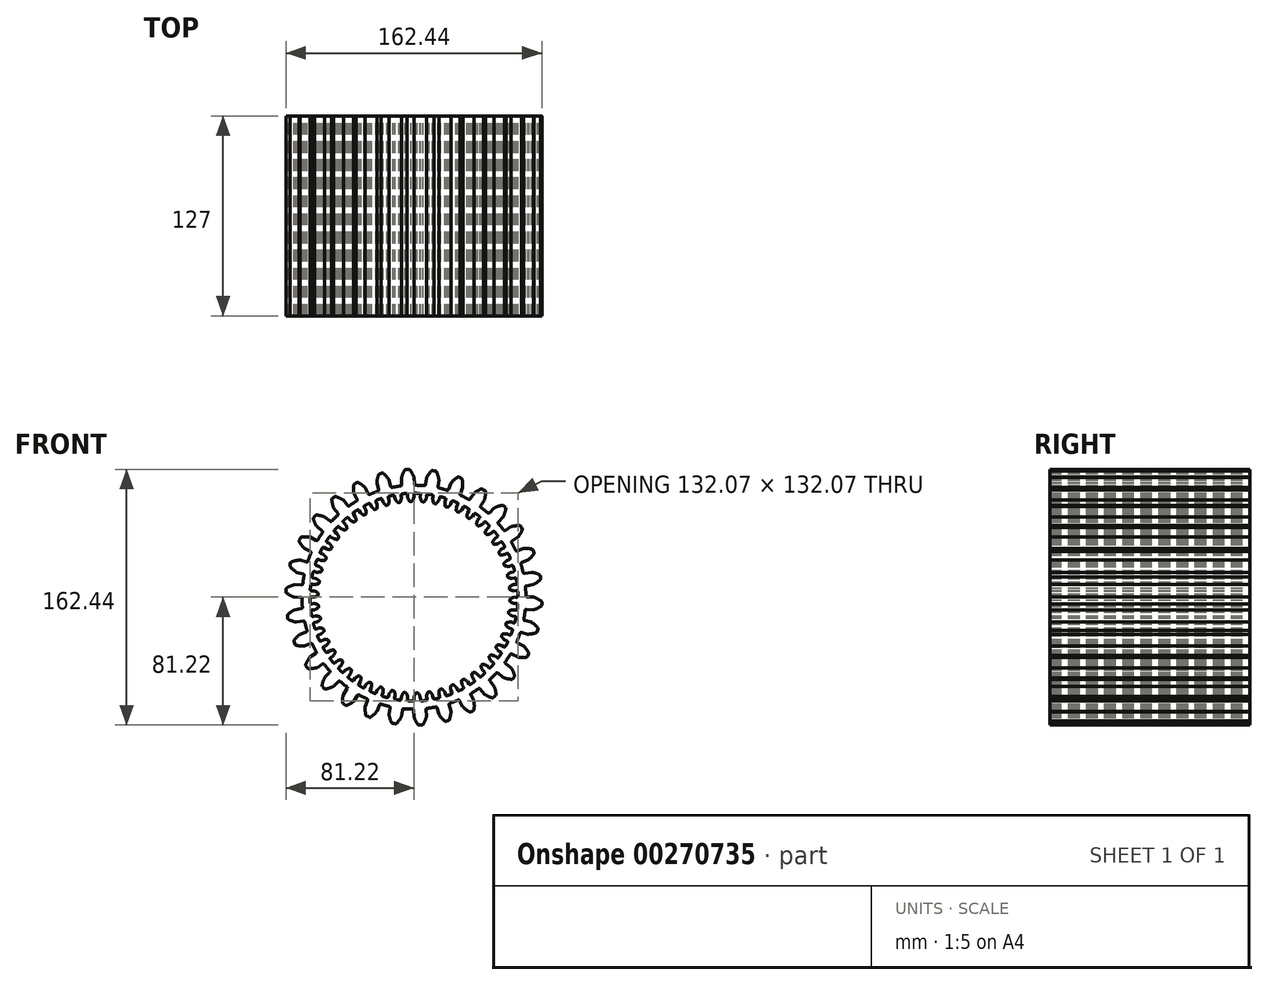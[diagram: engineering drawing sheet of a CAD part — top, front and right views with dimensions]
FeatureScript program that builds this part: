
annotation { "Feature Type Name" : "Feature", "Feature Type Description" : "" }
export const myFeature = defineFeature(function(context is Context, id is Id, definition is map)
    precondition{}
    {
        {
            var Q0;
            Q0=qCreatedBy(makeId("Front.planeOp"),FACE);
            var sketch = newSketch(context, id + "F0", { "sketchPlane" : qUnion([Q0])});
            skArc(sketch, "E0", {"start": v(-8.43, 70.62) * mm, "mid": v(-11.13, 70.24) * mm, "end": v(-13.8, 69.77) * mm});
            skArc(sketch, "E1", {"start": v(0, 76.2) * mm, "mid": v(-1.15, 78.65) * mm, "end": v(-2.63, 80.9) * mm});
            skLineSegment(sketch, "E2", {"start": v(-3.28, 81.21) * mm, "end": v(-4.25, 81.18) * mm});
            skLineSegment(sketch, "E3", {"start": v(0, 76.2) * mm, "end": v(0.23, 71.86) * mm});
            skLineSegment(sketch, "E4.MirrorCS", {"start": v(-5.23, 81.11) * mm, "end": v(-4.25, 81.18) * mm});
            skArc(sketch, "E5.MirrorCS", {"start": v(-7.97, 75.78) * mm, "mid": v(-7.08, 78.33) * mm, "end": v(-5.85, 80.74) * mm});
            skLineSegment(sketch, "E6.MirrorCS", {"start": v(-7.97, 75.78) * mm, "end": v(-7.74, 71.44) * mm});
            skPoint(sketch, "E7.visualSharp", {"position": v(-7.7, 70.7) * mm});
            skArc(sketch, "E7.filletArc", {"start": v(-8.43, 70.62) * mm, "mid": v(-7.92, 70.9) * mm, "end": v(-7.74, 71.44) * mm});
            skPoint(sketch, "E8.visualSharp", {"position": v(0.27, 71.12) * mm});
            skArc(sketch, "E8.filletArc", {"start": v(0.23, 71.86) * mm, "mid": v(0.47, 71.33) * mm, "end": v(1, 71.11) * mm});
            skPoint(sketch, "E9.visualSharp", {"position": v(-5.63, 81.08) * mm});
            skArc(sketch, "E9.filletArc", {"start": v(-5.23, 81.11) * mm, "mid": v(-5.58, 81) * mm, "end": v(-5.85, 80.74) * mm});
            skPoint(sketch, "E10.visualSharp", {"position": v(-2.88, 81.23) * mm});
            skArc(sketch, "E10.filletArc", {"start": v(-2.63, 80.9) * mm, "mid": v(-2.92, 81.14) * mm, "end": v(-3.28, 81.21) * mm});
            skArc(sketch, "E11.1.0", {"start": v(-22.93, 67.32) * mm, "mid": v(-22.49, 67.7) * mm, "end": v(-22.42, 68.27) * mm});
            skArc(sketch, "E11.1.1", {"start": v(-23.55, 72.47) * mm, "mid": v(-23.21, 75.15) * mm, "end": v(-22.5, 77.76) * mm});
            skArc(sketch, "E11.1.2", {"start": v(-21.98, 78.25) * mm, "mid": v(-22.3, 78.07) * mm, "end": v(-22.5, 77.76) * mm});
            skLineSegment(sketch, "E11.1.3", {"start": v(-21.98, 78.25) * mm, "end": v(-21.04, 78.52) * mm});
            skLineSegment(sketch, "E11.1.4", {"start": v(-20.1, 78.76) * mm, "end": v(-21.04, 78.52) * mm});
            skArc(sketch, "E11.1.5", {"start": v(-19.39, 78.6) * mm, "mid": v(-19.72, 78.76) * mm, "end": v(-20.1, 78.76) * mm});
            skArc(sketch, "E11.1.6", {"start": v(-15.84, 74.53) * mm, "mid": v(-17.47, 76.69) * mm, "end": v(-19.39, 78.6) * mm});
            skArc(sketch, "E11.1.7", {"start": v(-14.72, 70.34) * mm, "mid": v(-14.37, 69.87) * mm, "end": v(-13.8, 69.77) * mm});
            skLineSegment(sketch, "E11.1.8", {"start": v(-15.84, 74.53) * mm, "end": v(-14.72, 70.34) * mm});
            skLineSegment(sketch, "E11.1.9", {"start": v(-23.55, 72.47) * mm, "end": v(-22.42, 68.27) * mm});
            skArc(sketch, "E11.2.0", {"start": v(-36.42, 61.08) * mm, "mid": v(-36.07, 61.54) * mm, "end": v(-36.13, 62.12) * mm});
            skArc(sketch, "E11.2.1", {"start": v(-38.1, 66) * mm, "mid": v(-38.33, 68.68) * mm, "end": v(-38.18, 71.38) * mm});
            skArc(sketch, "E11.2.2", {"start": v(-37.77, 71.97) * mm, "mid": v(-38.05, 71.73) * mm, "end": v(-38.18, 71.38) * mm});
            skLineSegment(sketch, "E11.2.3", {"start": v(-37.77, 71.97) * mm, "end": v(-36.9, 72.43) * mm});
            skLineSegment(sketch, "E11.2.4", {"start": v(-36.03, 72.86) * mm, "end": v(-36.9, 72.43) * mm});
            skArc(sketch, "E11.2.5", {"start": v(-35.3, 72.84) * mm, "mid": v(-35.67, 72.94) * mm, "end": v(-36.03, 72.86) * mm});
            skArc(sketch, "E11.2.6", {"start": v(-31, 69.61) * mm, "mid": v(-33.03, 71.38) * mm, "end": v(-35.3, 72.84) * mm});
            skArc(sketch, "E11.2.7", {"start": v(-29.02, 65.74) * mm, "mid": v(-28.59, 65.36) * mm, "end": v(-28, 65.37) * mm});
            skLineSegment(sketch, "E11.2.8", {"start": v(-31, 69.61) * mm, "end": v(-29.02, 65.74) * mm});
            skLineSegment(sketch, "E11.2.9", {"start": v(-38.1, 66) * mm, "end": v(-36.13, 62.12) * mm});
            skArc(sketch, "E11.3.0", {"start": v(-48.33, 52.18) * mm, "mid": v(-48.08, 52.7) * mm, "end": v(-48.25, 53.25) * mm});
            skArc(sketch, "E11.3.1", {"start": v(-50.99, 56.63) * mm, "mid": v(-51.77, 59.21) * mm, "end": v(-52.18, 61.88) * mm});
            skArc(sketch, "E11.3.2", {"start": v(-51.9, 62.55) * mm, "mid": v(-52.13, 62.25) * mm, "end": v(-52.18, 61.88) * mm});
            skLineSegment(sketch, "E11.3.3", {"start": v(-51.9, 62.55) * mm, "end": v(-51.16, 63.18) * mm});
            skLineSegment(sketch, "E11.3.4", {"start": v(-50.4, 63.78) * mm, "end": v(-51.16, 63.18) * mm});
            skArc(sketch, "E11.3.5", {"start": v(-49.68, 63.91) * mm, "mid": v(-50.05, 63.93) * mm, "end": v(-50.4, 63.78) * mm});
            skArc(sketch, "E11.3.6", {"start": v(-44.79, 61.65) * mm, "mid": v(-47.15, 62.95) * mm, "end": v(-49.68, 63.91) * mm});
            skArc(sketch, "E11.3.7", {"start": v(-42.05, 58.27) * mm, "mid": v(-41.55, 57.98) * mm, "end": v(-40.99, 58.12) * mm});
            skLineSegment(sketch, "E11.3.8", {"start": v(-44.79, 61.65) * mm, "end": v(-42.05, 58.27) * mm});
            skLineSegment(sketch, "E11.3.9", {"start": v(-50.99, 56.63) * mm, "end": v(-48.25, 53.25) * mm});
            skArc(sketch, "E11.4.0", {"start": v(-58.12, 40.99) * mm, "mid": v(-57.98, 41.55) * mm, "end": v(-58.27, 42.05) * mm});
            skArc(sketch, "E11.4.1", {"start": v(-61.65, 44.79) * mm, "mid": v(-62.95, 47.15) * mm, "end": v(-63.91, 49.68) * mm});
            skArc(sketch, "E11.4.2", {"start": v(-63.78, 50.4) * mm, "mid": v(-63.93, 50.05) * mm, "end": v(-63.91, 49.68) * mm});
            skLineSegment(sketch, "E11.4.3", {"start": v(-63.78, 50.4) * mm, "end": v(-63.18, 51.16) * mm});
            skLineSegment(sketch, "E11.4.4", {"start": v(-62.55, 51.9) * mm, "end": v(-63.18, 51.16) * mm});
            skArc(sketch, "E11.4.5", {"start": v(-61.88, 52.18) * mm, "mid": v(-62.25, 52.13) * mm, "end": v(-62.55, 51.9) * mm});
            skArc(sketch, "E11.4.6", {"start": v(-56.63, 50.99) * mm, "mid": v(-59.21, 51.77) * mm, "end": v(-61.88, 52.18) * mm});
            skArc(sketch, "E11.4.7", {"start": v(-53.25, 48.25) * mm, "mid": v(-52.7, 48.08) * mm, "end": v(-52.18, 48.33) * mm});
            skLineSegment(sketch, "E11.4.8", {"start": v(-56.63, 50.99) * mm, "end": v(-53.25, 48.25) * mm});
            skLineSegment(sketch, "E11.4.9", {"start": v(-61.65, 44.79) * mm, "end": v(-58.27, 42.05) * mm});
            skArc(sketch, "E11.5.0", {"start": v(-65.37, 28) * mm, "mid": v(-65.36, 28.59) * mm, "end": v(-65.74, 29.02) * mm});
            skArc(sketch, "E11.5.1", {"start": v(-69.61, 31) * mm, "mid": v(-71.38, 33.03) * mm, "end": v(-72.84, 35.3) * mm});
            skArc(sketch, "E11.5.2", {"start": v(-72.86, 36.03) * mm, "mid": v(-72.94, 35.67) * mm, "end": v(-72.84, 35.3) * mm});
            skLineSegment(sketch, "E11.5.3", {"start": v(-72.86, 36.03) * mm, "end": v(-72.43, 36.9) * mm});
            skLineSegment(sketch, "E11.5.4", {"start": v(-71.97, 37.77) * mm, "end": v(-72.43, 36.9) * mm});
            skArc(sketch, "E11.5.5", {"start": v(-71.38, 38.18) * mm, "mid": v(-71.73, 38.05) * mm, "end": v(-71.97, 37.77) * mm});
            skArc(sketch, "E11.5.6", {"start": v(-66, 38.1) * mm, "mid": v(-68.68, 38.33) * mm, "end": v(-71.38, 38.18) * mm});
            skArc(sketch, "E11.5.7", {"start": v(-62.12, 36.13) * mm, "mid": v(-61.54, 36.07) * mm, "end": v(-61.08, 36.42) * mm});
            skLineSegment(sketch, "E11.5.8", {"start": v(-66, 38.1) * mm, "end": v(-62.12, 36.13) * mm});
            skLineSegment(sketch, "E11.5.9", {"start": v(-69.61, 31) * mm, "end": v(-65.74, 29.02) * mm});
            skArc(sketch, "E11.6.0", {"start": v(-69.77, 13.8) * mm, "mid": v(-69.87, 14.37) * mm, "end": v(-70.34, 14.72) * mm});
            skArc(sketch, "E11.6.1", {"start": v(-74.53, 15.84) * mm, "mid": v(-76.69, 17.47) * mm, "end": v(-78.6, 19.39) * mm});
            skArc(sketch, "E11.6.2", {"start": v(-78.76, 20.1) * mm, "mid": v(-78.76, 19.72) * mm, "end": v(-78.6, 19.39) * mm});
            skLineSegment(sketch, "E11.6.3", {"start": v(-78.76, 20.1) * mm, "end": v(-78.52, 21.04) * mm});
            skLineSegment(sketch, "E11.6.4", {"start": v(-78.25, 21.98) * mm, "end": v(-78.52, 21.04) * mm});
            skArc(sketch, "E11.6.5", {"start": v(-77.76, 22.5) * mm, "mid": v(-78.07, 22.3) * mm, "end": v(-78.25, 21.98) * mm});
            skArc(sketch, "E11.6.6", {"start": v(-72.47, 23.55) * mm, "mid": v(-75.15, 23.21) * mm, "end": v(-77.76, 22.5) * mm});
            skArc(sketch, "E11.6.7", {"start": v(-68.27, 22.42) * mm, "mid": v(-67.7, 22.49) * mm, "end": v(-67.32, 22.93) * mm});
            skLineSegment(sketch, "E11.6.8", {"start": v(-72.47, 23.55) * mm, "end": v(-68.27, 22.42) * mm});
            skLineSegment(sketch, "E11.6.9", {"start": v(-74.53, 15.84) * mm, "end": v(-70.34, 14.72) * mm});
            skArc(sketch, "E11.7.0", {"start": v(-71.11, -1) * mm, "mid": v(-71.33, -0.47) * mm, "end": v(-71.86, -0.23) * mm});
            skArc(sketch, "E11.7.1", {"start": v(-76.2, 0) * mm, "mid": v(-78.65, 1.15) * mm, "end": v(-80.9, 2.63) * mm});
            skArc(sketch, "E11.7.2", {"start": v(-81.21, 3.28) * mm, "mid": v(-81.14, 2.92) * mm, "end": v(-80.9, 2.63) * mm});
            skLineSegment(sketch, "E11.7.3", {"start": v(-81.21, 3.28) * mm, "end": v(-81.18, 4.25) * mm});
            skLineSegment(sketch, "E11.7.4", {"start": v(-81.11, 5.23) * mm, "end": v(-81.18, 4.25) * mm});
            skArc(sketch, "E11.7.5", {"start": v(-80.74, 5.85) * mm, "mid": v(-81, 5.58) * mm, "end": v(-81.11, 5.23) * mm});
            skArc(sketch, "E11.7.6", {"start": v(-75.78, 7.97) * mm, "mid": v(-78.33, 7.08) * mm, "end": v(-80.74, 5.85) * mm});
            skArc(sketch, "E11.7.7", {"start": v(-71.44, 7.74) * mm, "mid": v(-70.9, 7.92) * mm, "end": v(-70.62, 8.43) * mm});
            skLineSegment(sketch, "E11.7.8", {"start": v(-75.78, 7.97) * mm, "end": v(-71.44, 7.74) * mm});
            skLineSegment(sketch, "E11.7.9", {"start": v(-76.2, 0) * mm, "end": v(-71.86, -0.23) * mm});
            skArc(sketch, "E11.8.0", {"start": v(-69.35, -15.77) * mm, "mid": v(-69.68, -15.29) * mm, "end": v(-70.24, -15.16) * mm});
            skArc(sketch, "E11.8.1", {"start": v(-74.53, -15.84) * mm, "mid": v(-77.17, -15.23) * mm, "end": v(-79.68, -14.25) * mm});
            skArc(sketch, "E11.8.2", {"start": v(-80.12, -13.68) * mm, "mid": v(-79.97, -14.02) * mm, "end": v(-79.68, -14.25) * mm});
            skLineSegment(sketch, "E11.8.3", {"start": v(-80.12, -13.68) * mm, "end": v(-80.3, -12.72) * mm});
            skLineSegment(sketch, "E11.8.4", {"start": v(-80.43, -11.75) * mm, "end": v(-80.3, -12.72) * mm});
            skArc(sketch, "E11.8.5", {"start": v(-80.19, -11.07) * mm, "mid": v(-80.4, -11.38) * mm, "end": v(-80.43, -11.75) * mm});
            skArc(sketch, "E11.8.6", {"start": v(-75.78, -7.97) * mm, "mid": v(-78.1, -9.36) * mm, "end": v(-80.19, -11.07) * mm});
            skArc(sketch, "E11.8.7", {"start": v(-71.49, -7.29) * mm, "mid": v(-71, -7) * mm, "end": v(-70.83, -6.44) * mm});
            skLineSegment(sketch, "E11.8.8", {"start": v(-75.78, -7.97) * mm, "end": v(-71.49, -7.29) * mm});
            skLineSegment(sketch, "E11.8.9", {"start": v(-74.53, -15.84) * mm, "end": v(-70.24, -15.16) * mm});
            skArc(sketch, "E11.9.0", {"start": v(-64.56, -29.84) * mm, "mid": v(-64.98, -29.44) * mm, "end": v(-65.55, -29.44) * mm});
            skArc(sketch, "E11.9.1", {"start": v(-69.61, -31) * mm, "mid": v(-72.31, -30.94) * mm, "end": v(-74.98, -30.5) * mm});
            skArc(sketch, "E11.9.2", {"start": v(-75.53, -30.04) * mm, "mid": v(-75.31, -30.34) * mm, "end": v(-74.98, -30.5) * mm});
            skLineSegment(sketch, "E11.9.3", {"start": v(-75.53, -30.04) * mm, "end": v(-75.9, -29.13) * mm});
            skLineSegment(sketch, "E11.9.4", {"start": v(-76.23, -28.22) * mm, "end": v(-75.9, -29.13) * mm});
            skArc(sketch, "E11.9.5", {"start": v(-76.13, -27.5) * mm, "mid": v(-76.27, -27.85) * mm, "end": v(-76.23, -28.22) * mm});
            skArc(sketch, "E11.9.6", {"start": v(-72.47, -23.55) * mm, "mid": v(-74.44, -25.4) * mm, "end": v(-76.13, -27.5) * mm});
            skArc(sketch, "E11.9.7", {"start": v(-68.41, -21.99) * mm, "mid": v(-67.99, -21.6) * mm, "end": v(-67.94, -21.02) * mm});
            skLineSegment(sketch, "E11.9.8", {"start": v(-72.47, -23.55) * mm, "end": v(-68.41, -21.99) * mm});
            skLineSegment(sketch, "E11.9.9", {"start": v(-69.61, -31) * mm, "end": v(-65.55, -29.44) * mm});
            skArc(sketch, "E11.10.0", {"start": v(-56.94, -42.61) * mm, "mid": v(-57.43, -42.3) * mm, "end": v(-58, -42.42) * mm});
            skArc(sketch, "E11.10.1", {"start": v(-61.65, -44.79) * mm, "mid": v(-64.3, -45.3) * mm, "end": v(-67, -45.43) * mm});
            skArc(sketch, "E11.10.2", {"start": v(-67.63, -45.08) * mm, "mid": v(-67.36, -45.33) * mm, "end": v(-67, -45.43) * mm});
            skLineSegment(sketch, "E11.10.3", {"start": v(-67.63, -45.08) * mm, "end": v(-68.18, -44.27) * mm});
            skLineSegment(sketch, "E11.10.4", {"start": v(-68.7, -43.45) * mm, "end": v(-68.18, -44.27) * mm});
            skArc(sketch, "E11.10.5", {"start": v(-68.75, -42.73) * mm, "mid": v(-68.81, -43.1) * mm, "end": v(-68.7, -43.45) * mm});
            skArc(sketch, "E11.10.6", {"start": v(-66, -38.1) * mm, "mid": v(-67.54, -40.32) * mm, "end": v(-68.75, -42.73) * mm});
            skArc(sketch, "E11.10.7", {"start": v(-62.35, -35.73) * mm, "mid": v(-62.01, -35.26) * mm, "end": v(-62.09, -34.69) * mm});
            skLineSegment(sketch, "E11.10.8", {"start": v(-66, -38.1) * mm, "end": v(-62.35, -35.73) * mm});
            skLineSegment(sketch, "E11.10.9", {"start": v(-61.65, -44.79) * mm, "end": v(-58, -42.42) * mm});
            skArc(sketch, "E11.11.0", {"start": v(-46.84, -53.52) * mm, "mid": v(-47.38, -53.32) * mm, "end": v(-47.91, -53.55) * mm});
            skArc(sketch, "E11.11.1", {"start": v(-50.99, -56.63) * mm, "mid": v(-53.48, -57.68) * mm, "end": v(-56.09, -58.37) * mm});
            skArc(sketch, "E11.11.2", {"start": v(-56.78, -58.16) * mm, "mid": v(-56.46, -58.35) * mm, "end": v(-56.09, -58.37) * mm});
            skLineSegment(sketch, "E11.11.3", {"start": v(-56.78, -58.16) * mm, "end": v(-57.48, -57.48) * mm});
            skLineSegment(sketch, "E11.11.4", {"start": v(-58.16, -56.78) * mm, "end": v(-57.48, -57.48) * mm});
            skArc(sketch, "E11.11.5", {"start": v(-58.37, -56.09) * mm, "mid": v(-58.35, -56.46) * mm, "end": v(-58.16, -56.78) * mm});
            skArc(sketch, "E11.11.6", {"start": v(-56.63, -50.99) * mm, "mid": v(-57.68, -53.48) * mm, "end": v(-58.37, -56.09) * mm});
            skArc(sketch, "E11.11.7", {"start": v(-53.55, -47.91) * mm, "mid": v(-53.32, -47.38) * mm, "end": v(-53.52, -46.84) * mm});
            skLineSegment(sketch, "E11.11.8", {"start": v(-56.63, -50.99) * mm, "end": v(-53.55, -47.91) * mm});
            skLineSegment(sketch, "E11.11.9", {"start": v(-50.99, -56.63) * mm, "end": v(-47.91, -53.55) * mm});
            skArc(sketch, "E11.12.0", {"start": v(-34.69, -62.09) * mm, "mid": v(-35.26, -62.01) * mm, "end": v(-35.73, -62.35) * mm});
            skArc(sketch, "E11.12.1", {"start": v(-38.1, -66) * mm, "mid": v(-40.32, -67.54) * mm, "end": v(-42.73, -68.75) * mm});
            skArc(sketch, "E11.12.2", {"start": v(-43.45, -68.7) * mm, "mid": v(-43.1, -68.81) * mm, "end": v(-42.73, -68.75) * mm});
            skLineSegment(sketch, "E11.12.3", {"start": v(-43.45, -68.7) * mm, "end": v(-44.27, -68.18) * mm});
            skLineSegment(sketch, "E11.12.4", {"start": v(-45.08, -67.63) * mm, "end": v(-44.27, -68.18) * mm});
            skArc(sketch, "E11.12.5", {"start": v(-45.43, -67) * mm, "mid": v(-45.33, -67.36) * mm, "end": v(-45.08, -67.63) * mm});
            skArc(sketch, "E11.12.6", {"start": v(-44.79, -61.65) * mm, "mid": v(-45.3, -64.3) * mm, "end": v(-45.43, -67) * mm});
            skArc(sketch, "E11.12.7", {"start": v(-42.42, -58) * mm, "mid": v(-42.3, -57.43) * mm, "end": v(-42.61, -56.94) * mm});
            skLineSegment(sketch, "E11.12.8", {"start": v(-44.79, -61.65) * mm, "end": v(-42.42, -58) * mm});
            skLineSegment(sketch, "E11.12.9", {"start": v(-38.1, -66) * mm, "end": v(-35.73, -62.35) * mm});
            skArc(sketch, "E11.13.0", {"start": v(-21.02, -67.94) * mm, "mid": v(-21.6, -67.99) * mm, "end": v(-21.99, -68.41) * mm});
            skArc(sketch, "E11.13.1", {"start": v(-23.55, -72.47) * mm, "mid": v(-25.4, -74.44) * mm, "end": v(-27.5, -76.13) * mm});
            skArc(sketch, "E11.13.2", {"start": v(-28.22, -76.23) * mm, "mid": v(-27.85, -76.27) * mm, "end": v(-27.5, -76.13) * mm});
            skLineSegment(sketch, "E11.13.3", {"start": v(-28.22, -76.23) * mm, "end": v(-29.13, -75.9) * mm});
            skLineSegment(sketch, "E11.13.4", {"start": v(-30.04, -75.53) * mm, "end": v(-29.13, -75.9) * mm});
            skArc(sketch, "E11.13.5", {"start": v(-30.5, -74.98) * mm, "mid": v(-30.34, -75.31) * mm, "end": v(-30.04, -75.53) * mm});
            skArc(sketch, "E11.13.6", {"start": v(-31, -69.61) * mm, "mid": v(-30.94, -72.31) * mm, "end": v(-30.5, -74.98) * mm});
            skArc(sketch, "E11.13.7", {"start": v(-29.44, -65.55) * mm, "mid": v(-29.44, -64.98) * mm, "end": v(-29.84, -64.56) * mm});
            skLineSegment(sketch, "E11.13.8", {"start": v(-31, -69.61) * mm, "end": v(-29.44, -65.55) * mm});
            skLineSegment(sketch, "E11.13.9", {"start": v(-23.55, -72.47) * mm, "end": v(-21.99, -68.41) * mm});
            skArc(sketch, "E11.14.0", {"start": v(-6.44, -70.83) * mm, "mid": v(-7, -71) * mm, "end": v(-7.29, -71.49) * mm});
            skArc(sketch, "E11.14.1", {"start": v(-7.97, -75.78) * mm, "mid": v(-9.36, -78.1) * mm, "end": v(-11.07, -80.19) * mm});
            skArc(sketch, "E11.14.2", {"start": v(-11.75, -80.43) * mm, "mid": v(-11.38, -80.4) * mm, "end": v(-11.07, -80.19) * mm});
            skLineSegment(sketch, "E11.14.3", {"start": v(-11.75, -80.43) * mm, "end": v(-12.72, -80.3) * mm});
            skLineSegment(sketch, "E11.14.4", {"start": v(-13.68, -80.12) * mm, "end": v(-12.72, -80.3) * mm});
            skArc(sketch, "E11.14.5", {"start": v(-14.25, -79.68) * mm, "mid": v(-14.02, -79.97) * mm, "end": v(-13.68, -80.12) * mm});
            skArc(sketch, "E11.14.6", {"start": v(-15.84, -74.53) * mm, "mid": v(-15.23, -77.17) * mm, "end": v(-14.25, -79.68) * mm});
            skArc(sketch, "E11.14.7", {"start": v(-15.16, -70.24) * mm, "mid": v(-15.29, -69.68) * mm, "end": v(-15.77, -69.35) * mm});
            skLineSegment(sketch, "E11.14.8", {"start": v(-15.84, -74.53) * mm, "end": v(-15.16, -70.24) * mm});
            skLineSegment(sketch, "E11.14.9", {"start": v(-7.97, -75.78) * mm, "end": v(-7.29, -71.49) * mm});
            skArc(sketch, "E11.15.0", {"start": v(8.43, -70.62) * mm, "mid": v(7.92, -70.9) * mm, "end": v(7.74, -71.44) * mm});
            skArc(sketch, "E11.15.1", {"start": v(7.97, -75.78) * mm, "mid": v(7.08, -78.33) * mm, "end": v(5.85, -80.74) * mm});
            skArc(sketch, "E11.15.2", {"start": v(5.23, -81.11) * mm, "mid": v(5.58, -81) * mm, "end": v(5.85, -80.74) * mm});
            skLineSegment(sketch, "E11.15.3", {"start": v(5.23, -81.11) * mm, "end": v(4.25, -81.18) * mm});
            skLineSegment(sketch, "E11.15.4", {"start": v(3.28, -81.21) * mm, "end": v(4.25, -81.18) * mm});
            skArc(sketch, "E11.15.5", {"start": v(2.63, -80.9) * mm, "mid": v(2.92, -81.14) * mm, "end": v(3.28, -81.21) * mm});
            skArc(sketch, "E11.15.6", {"start": v(0, -76.2) * mm, "mid": v(1.15, -78.65) * mm, "end": v(2.63, -80.9) * mm});
            skArc(sketch, "E11.15.7", {"start": v(-0.23, -71.86) * mm, "mid": v(-0.47, -71.33) * mm, "end": v(-1, -71.11) * mm});
            skLineSegment(sketch, "E11.15.8", {"start": v(0, -76.2) * mm, "end": v(-0.23, -71.86) * mm});
            skLineSegment(sketch, "E11.15.9", {"start": v(7.97, -75.78) * mm, "end": v(7.74, -71.44) * mm});
            skArc(sketch, "E11.16.0", {"start": v(22.93, -67.32) * mm, "mid": v(22.49, -67.7) * mm, "end": v(22.42, -68.27) * mm});
            skArc(sketch, "E11.16.1", {"start": v(23.55, -72.47) * mm, "mid": v(23.21, -75.15) * mm, "end": v(22.5, -77.76) * mm});
            skArc(sketch, "E11.16.2", {"start": v(21.98, -78.25) * mm, "mid": v(22.3, -78.07) * mm, "end": v(22.5, -77.76) * mm});
            skLineSegment(sketch, "E11.16.3", {"start": v(21.98, -78.25) * mm, "end": v(21.04, -78.52) * mm});
            skLineSegment(sketch, "E11.16.4", {"start": v(20.1, -78.76) * mm, "end": v(21.04, -78.52) * mm});
            skArc(sketch, "E11.16.5", {"start": v(19.39, -78.6) * mm, "mid": v(19.72, -78.76) * mm, "end": v(20.1, -78.76) * mm});
            skArc(sketch, "E11.16.6", {"start": v(15.84, -74.53) * mm, "mid": v(17.47, -76.69) * mm, "end": v(19.39, -78.6) * mm});
            skArc(sketch, "E11.16.7", {"start": v(14.72, -70.34) * mm, "mid": v(14.37, -69.87) * mm, "end": v(13.8, -69.77) * mm});
            skLineSegment(sketch, "E11.16.8", {"start": v(15.84, -74.53) * mm, "end": v(14.72, -70.34) * mm});
            skLineSegment(sketch, "E11.16.9", {"start": v(23.55, -72.47) * mm, "end": v(22.42, -68.27) * mm});
            skArc(sketch, "E11.17.0", {"start": v(36.42, -61.08) * mm, "mid": v(36.07, -61.54) * mm, "end": v(36.13, -62.12) * mm});
            skArc(sketch, "E11.17.1", {"start": v(38.1, -66) * mm, "mid": v(38.33, -68.68) * mm, "end": v(38.18, -71.38) * mm});
            skArc(sketch, "E11.17.2", {"start": v(37.77, -71.97) * mm, "mid": v(38.05, -71.73) * mm, "end": v(38.18, -71.38) * mm});
            skLineSegment(sketch, "E11.17.3", {"start": v(37.77, -71.97) * mm, "end": v(36.9, -72.43) * mm});
            skLineSegment(sketch, "E11.17.4", {"start": v(36.03, -72.86) * mm, "end": v(36.9, -72.43) * mm});
            skArc(sketch, "E11.17.5", {"start": v(35.3, -72.84) * mm, "mid": v(35.67, -72.94) * mm, "end": v(36.03, -72.86) * mm});
            skArc(sketch, "E11.17.6", {"start": v(31, -69.61) * mm, "mid": v(33.03, -71.38) * mm, "end": v(35.3, -72.84) * mm});
            skArc(sketch, "E11.17.7", {"start": v(29.02, -65.74) * mm, "mid": v(28.59, -65.36) * mm, "end": v(28, -65.37) * mm});
            skLineSegment(sketch, "E11.17.8", {"start": v(31, -69.61) * mm, "end": v(29.02, -65.74) * mm});
            skLineSegment(sketch, "E11.17.9", {"start": v(38.1, -66) * mm, "end": v(36.13, -62.12) * mm});
            skArc(sketch, "E11.18.0", {"start": v(48.33, -52.18) * mm, "mid": v(48.08, -52.7) * mm, "end": v(48.25, -53.25) * mm});
            skArc(sketch, "E11.18.1", {"start": v(50.99, -56.63) * mm, "mid": v(51.77, -59.21) * mm, "end": v(52.18, -61.88) * mm});
            skArc(sketch, "E11.18.2", {"start": v(51.9, -62.55) * mm, "mid": v(52.13, -62.25) * mm, "end": v(52.18, -61.88) * mm});
            skLineSegment(sketch, "E11.18.3", {"start": v(51.9, -62.55) * mm, "end": v(51.16, -63.18) * mm});
            skLineSegment(sketch, "E11.18.4", {"start": v(50.4, -63.78) * mm, "end": v(51.16, -63.18) * mm});
            skArc(sketch, "E11.18.5", {"start": v(49.68, -63.91) * mm, "mid": v(50.05, -63.93) * mm, "end": v(50.4, -63.78) * mm});
            skArc(sketch, "E11.18.6", {"start": v(44.79, -61.65) * mm, "mid": v(47.15, -62.95) * mm, "end": v(49.68, -63.91) * mm});
            skArc(sketch, "E11.18.7", {"start": v(42.05, -58.27) * mm, "mid": v(41.55, -57.98) * mm, "end": v(40.99, -58.12) * mm});
            skLineSegment(sketch, "E11.18.8", {"start": v(44.79, -61.65) * mm, "end": v(42.05, -58.27) * mm});
            skLineSegment(sketch, "E11.18.9", {"start": v(50.99, -56.63) * mm, "end": v(48.25, -53.25) * mm});
            skArc(sketch, "E11.19.0", {"start": v(58.12, -40.99) * mm, "mid": v(57.98, -41.55) * mm, "end": v(58.27, -42.05) * mm});
            skArc(sketch, "E11.19.1", {"start": v(61.65, -44.79) * mm, "mid": v(62.95, -47.15) * mm, "end": v(63.91, -49.68) * mm});
            skArc(sketch, "E11.19.2", {"start": v(63.78, -50.4) * mm, "mid": v(63.93, -50.05) * mm, "end": v(63.91, -49.68) * mm});
            skLineSegment(sketch, "E11.19.3", {"start": v(63.78, -50.4) * mm, "end": v(63.18, -51.16) * mm});
            skLineSegment(sketch, "E11.19.4", {"start": v(62.55, -51.9) * mm, "end": v(63.18, -51.16) * mm});
            skArc(sketch, "E11.19.5", {"start": v(61.88, -52.18) * mm, "mid": v(62.25, -52.13) * mm, "end": v(62.55, -51.9) * mm});
            skArc(sketch, "E11.19.6", {"start": v(56.63, -50.99) * mm, "mid": v(59.21, -51.77) * mm, "end": v(61.88, -52.18) * mm});
            skArc(sketch, "E11.19.7", {"start": v(53.25, -48.25) * mm, "mid": v(52.7, -48.08) * mm, "end": v(52.18, -48.33) * mm});
            skLineSegment(sketch, "E11.19.8", {"start": v(56.63, -50.99) * mm, "end": v(53.25, -48.25) * mm});
            skLineSegment(sketch, "E11.19.9", {"start": v(61.65, -44.79) * mm, "end": v(58.27, -42.05) * mm});
            skArc(sketch, "E11.20.0", {"start": v(65.37, -28) * mm, "mid": v(65.36, -28.59) * mm, "end": v(65.74, -29.02) * mm});
            skArc(sketch, "E11.20.1", {"start": v(69.61, -31) * mm, "mid": v(71.38, -33.03) * mm, "end": v(72.84, -35.3) * mm});
            skArc(sketch, "E11.20.2", {"start": v(72.86, -36.03) * mm, "mid": v(72.94, -35.67) * mm, "end": v(72.84, -35.3) * mm});
            skLineSegment(sketch, "E11.20.3", {"start": v(72.86, -36.03) * mm, "end": v(72.43, -36.9) * mm});
            skLineSegment(sketch, "E11.20.4", {"start": v(71.97, -37.77) * mm, "end": v(72.43, -36.9) * mm});
            skArc(sketch, "E11.20.5", {"start": v(71.38, -38.18) * mm, "mid": v(71.73, -38.05) * mm, "end": v(71.97, -37.77) * mm});
            skArc(sketch, "E11.20.6", {"start": v(66, -38.1) * mm, "mid": v(68.68, -38.33) * mm, "end": v(71.38, -38.18) * mm});
            skArc(sketch, "E11.20.7", {"start": v(62.12, -36.13) * mm, "mid": v(61.54, -36.07) * mm, "end": v(61.08, -36.42) * mm});
            skLineSegment(sketch, "E11.20.8", {"start": v(66, -38.1) * mm, "end": v(62.12, -36.13) * mm});
            skLineSegment(sketch, "E11.20.9", {"start": v(69.61, -31) * mm, "end": v(65.74, -29.02) * mm});
            skArc(sketch, "E11.21.0", {"start": v(69.77, -13.8) * mm, "mid": v(69.87, -14.37) * mm, "end": v(70.34, -14.72) * mm});
            skArc(sketch, "E11.21.1", {"start": v(74.53, -15.84) * mm, "mid": v(76.69, -17.47) * mm, "end": v(78.6, -19.39) * mm});
            skArc(sketch, "E11.21.2", {"start": v(78.76, -20.1) * mm, "mid": v(78.76, -19.72) * mm, "end": v(78.6, -19.39) * mm});
            skLineSegment(sketch, "E11.21.3", {"start": v(78.76, -20.1) * mm, "end": v(78.52, -21.04) * mm});
            skLineSegment(sketch, "E11.21.4", {"start": v(78.25, -21.98) * mm, "end": v(78.52, -21.04) * mm});
            skArc(sketch, "E11.21.5", {"start": v(77.76, -22.5) * mm, "mid": v(78.07, -22.3) * mm, "end": v(78.25, -21.98) * mm});
            skArc(sketch, "E11.21.6", {"start": v(72.47, -23.55) * mm, "mid": v(75.15, -23.21) * mm, "end": v(77.76, -22.5) * mm});
            skArc(sketch, "E11.21.7", {"start": v(68.27, -22.42) * mm, "mid": v(67.7, -22.49) * mm, "end": v(67.32, -22.93) * mm});
            skLineSegment(sketch, "E11.21.8", {"start": v(72.47, -23.55) * mm, "end": v(68.27, -22.42) * mm});
            skLineSegment(sketch, "E11.21.9", {"start": v(74.53, -15.84) * mm, "end": v(70.34, -14.72) * mm});
            skArc(sketch, "E11.22.0", {"start": v(71.11, 1) * mm, "mid": v(71.33, 0.47) * mm, "end": v(71.86, 0.23) * mm});
            skArc(sketch, "E11.22.1", {"start": v(76.2, 0) * mm, "mid": v(78.65, -1.15) * mm, "end": v(80.9, -2.63) * mm});
            skArc(sketch, "E11.22.2", {"start": v(81.21, -3.28) * mm, "mid": v(81.14, -2.92) * mm, "end": v(80.9, -2.63) * mm});
            skLineSegment(sketch, "E11.22.3", {"start": v(81.21, -3.28) * mm, "end": v(81.18, -4.25) * mm});
            skLineSegment(sketch, "E11.22.4", {"start": v(81.11, -5.23) * mm, "end": v(81.18, -4.25) * mm});
            skArc(sketch, "E11.22.5", {"start": v(80.74, -5.85) * mm, "mid": v(81, -5.58) * mm, "end": v(81.11, -5.23) * mm});
            skArc(sketch, "E11.22.6", {"start": v(75.78, -7.97) * mm, "mid": v(78.33, -7.08) * mm, "end": v(80.74, -5.85) * mm});
            skArc(sketch, "E11.22.7", {"start": v(71.44, -7.74) * mm, "mid": v(70.9, -7.92) * mm, "end": v(70.62, -8.43) * mm});
            skLineSegment(sketch, "E11.22.8", {"start": v(75.78, -7.97) * mm, "end": v(71.44, -7.74) * mm});
            skLineSegment(sketch, "E11.22.9", {"start": v(76.2, 0) * mm, "end": v(71.86, 0.23) * mm});
            skArc(sketch, "E11.23.0", {"start": v(69.35, 15.77) * mm, "mid": v(69.68, 15.29) * mm, "end": v(70.24, 15.16) * mm});
            skArc(sketch, "E11.23.1", {"start": v(74.53, 15.84) * mm, "mid": v(77.17, 15.23) * mm, "end": v(79.68, 14.25) * mm});
            skArc(sketch, "E11.23.2", {"start": v(80.12, 13.68) * mm, "mid": v(79.97, 14.02) * mm, "end": v(79.68, 14.25) * mm});
            skLineSegment(sketch, "E11.23.3", {"start": v(80.12, 13.68) * mm, "end": v(80.3, 12.72) * mm});
            skLineSegment(sketch, "E11.23.4", {"start": v(80.43, 11.75) * mm, "end": v(80.3, 12.72) * mm});
            skArc(sketch, "E11.23.5", {"start": v(80.19, 11.07) * mm, "mid": v(80.4, 11.38) * mm, "end": v(80.43, 11.75) * mm});
            skArc(sketch, "E11.23.6", {"start": v(75.78, 7.97) * mm, "mid": v(78.1, 9.36) * mm, "end": v(80.19, 11.07) * mm});
            skArc(sketch, "E11.23.7", {"start": v(71.49, 7.29) * mm, "mid": v(71, 7) * mm, "end": v(70.83, 6.44) * mm});
            skLineSegment(sketch, "E11.23.8", {"start": v(75.78, 7.97) * mm, "end": v(71.49, 7.29) * mm});
            skLineSegment(sketch, "E11.23.9", {"start": v(74.53, 15.84) * mm, "end": v(70.24, 15.16) * mm});
            skArc(sketch, "E11.24.0", {"start": v(64.56, 29.84) * mm, "mid": v(64.98, 29.44) * mm, "end": v(65.55, 29.44) * mm});
            skArc(sketch, "E11.24.1", {"start": v(69.61, 31) * mm, "mid": v(72.31, 30.94) * mm, "end": v(74.98, 30.5) * mm});
            skArc(sketch, "E11.24.2", {"start": v(75.53, 30.04) * mm, "mid": v(75.31, 30.34) * mm, "end": v(74.98, 30.5) * mm});
            skLineSegment(sketch, "E11.24.3", {"start": v(75.53, 30.04) * mm, "end": v(75.9, 29.13) * mm});
            skLineSegment(sketch, "E11.24.4", {"start": v(76.23, 28.22) * mm, "end": v(75.9, 29.13) * mm});
            skArc(sketch, "E11.24.5", {"start": v(76.13, 27.5) * mm, "mid": v(76.27, 27.85) * mm, "end": v(76.23, 28.22) * mm});
            skArc(sketch, "E11.24.6", {"start": v(72.47, 23.55) * mm, "mid": v(74.44, 25.4) * mm, "end": v(76.13, 27.5) * mm});
            skArc(sketch, "E11.24.7", {"start": v(68.41, 21.99) * mm, "mid": v(67.99, 21.6) * mm, "end": v(67.94, 21.02) * mm});
            skLineSegment(sketch, "E11.24.8", {"start": v(72.47, 23.55) * mm, "end": v(68.41, 21.99) * mm});
            skLineSegment(sketch, "E11.24.9", {"start": v(69.61, 31) * mm, "end": v(65.55, 29.44) * mm});
            skArc(sketch, "E11.25.0", {"start": v(56.94, 42.61) * mm, "mid": v(57.43, 42.3) * mm, "end": v(58, 42.42) * mm});
            skArc(sketch, "E11.25.1", {"start": v(61.65, 44.79) * mm, "mid": v(64.3, 45.3) * mm, "end": v(67, 45.43) * mm});
            skArc(sketch, "E11.25.2", {"start": v(67.63, 45.08) * mm, "mid": v(67.36, 45.33) * mm, "end": v(67, 45.43) * mm});
            skLineSegment(sketch, "E11.25.3", {"start": v(67.63, 45.08) * mm, "end": v(68.18, 44.27) * mm});
            skLineSegment(sketch, "E11.25.4", {"start": v(68.7, 43.45) * mm, "end": v(68.18, 44.27) * mm});
            skArc(sketch, "E11.25.5", {"start": v(68.75, 42.73) * mm, "mid": v(68.81, 43.1) * mm, "end": v(68.7, 43.45) * mm});
            skArc(sketch, "E11.25.6", {"start": v(66, 38.1) * mm, "mid": v(67.54, 40.32) * mm, "end": v(68.75, 42.73) * mm});
            skArc(sketch, "E11.25.7", {"start": v(62.35, 35.73) * mm, "mid": v(62.01, 35.26) * mm, "end": v(62.09, 34.69) * mm});
            skLineSegment(sketch, "E11.25.8", {"start": v(66, 38.1) * mm, "end": v(62.35, 35.73) * mm});
            skLineSegment(sketch, "E11.25.9", {"start": v(61.65, 44.79) * mm, "end": v(58, 42.42) * mm});
            skArc(sketch, "E11.26.0", {"start": v(46.84, 53.52) * mm, "mid": v(47.38, 53.32) * mm, "end": v(47.91, 53.55) * mm});
            skArc(sketch, "E11.26.1", {"start": v(50.99, 56.63) * mm, "mid": v(53.48, 57.68) * mm, "end": v(56.09, 58.37) * mm});
            skArc(sketch, "E11.26.2", {"start": v(56.78, 58.16) * mm, "mid": v(56.46, 58.35) * mm, "end": v(56.09, 58.37) * mm});
            skLineSegment(sketch, "E11.26.3", {"start": v(56.78, 58.16) * mm, "end": v(57.48, 57.48) * mm});
            skLineSegment(sketch, "E11.26.4", {"start": v(58.16, 56.78) * mm, "end": v(57.48, 57.48) * mm});
            skArc(sketch, "E11.26.5", {"start": v(58.37, 56.09) * mm, "mid": v(58.35, 56.46) * mm, "end": v(58.16, 56.78) * mm});
            skArc(sketch, "E11.26.6", {"start": v(56.63, 50.99) * mm, "mid": v(57.68, 53.48) * mm, "end": v(58.37, 56.09) * mm});
            skArc(sketch, "E11.26.7", {"start": v(53.55, 47.91) * mm, "mid": v(53.32, 47.38) * mm, "end": v(53.52, 46.84) * mm});
            skLineSegment(sketch, "E11.26.8", {"start": v(56.63, 50.99) * mm, "end": v(53.55, 47.91) * mm});
            skLineSegment(sketch, "E11.26.9", {"start": v(50.99, 56.63) * mm, "end": v(47.91, 53.55) * mm});
            skArc(sketch, "E11.27.0", {"start": v(34.69, 62.09) * mm, "mid": v(35.26, 62.01) * mm, "end": v(35.73, 62.35) * mm});
            skArc(sketch, "E11.27.1", {"start": v(38.1, 66) * mm, "mid": v(40.32, 67.54) * mm, "end": v(42.73, 68.75) * mm});
            skArc(sketch, "E11.27.2", {"start": v(43.45, 68.7) * mm, "mid": v(43.1, 68.81) * mm, "end": v(42.73, 68.75) * mm});
            skLineSegment(sketch, "E11.27.3", {"start": v(43.45, 68.7) * mm, "end": v(44.27, 68.18) * mm});
            skLineSegment(sketch, "E11.27.4", {"start": v(45.08, 67.63) * mm, "end": v(44.27, 68.18) * mm});
            skArc(sketch, "E11.27.5", {"start": v(45.43, 67) * mm, "mid": v(45.33, 67.36) * mm, "end": v(45.08, 67.63) * mm});
            skArc(sketch, "E11.27.6", {"start": v(44.79, 61.65) * mm, "mid": v(45.3, 64.3) * mm, "end": v(45.43, 67) * mm});
            skArc(sketch, "E11.27.7", {"start": v(42.42, 58) * mm, "mid": v(42.3, 57.43) * mm, "end": v(42.61, 56.94) * mm});
            skLineSegment(sketch, "E11.27.8", {"start": v(44.79, 61.65) * mm, "end": v(42.42, 58) * mm});
            skLineSegment(sketch, "E11.27.9", {"start": v(38.1, 66) * mm, "end": v(35.73, 62.35) * mm});
            skArc(sketch, "E11.28.0", {"start": v(21.02, 67.94) * mm, "mid": v(21.6, 67.99) * mm, "end": v(21.99, 68.41) * mm});
            skArc(sketch, "E11.28.1", {"start": v(23.55, 72.47) * mm, "mid": v(25.4, 74.44) * mm, "end": v(27.5, 76.13) * mm});
            skArc(sketch, "E11.28.2", {"start": v(28.22, 76.23) * mm, "mid": v(27.85, 76.27) * mm, "end": v(27.5, 76.13) * mm});
            skLineSegment(sketch, "E11.28.3", {"start": v(28.22, 76.23) * mm, "end": v(29.13, 75.9) * mm});
            skLineSegment(sketch, "E11.28.4", {"start": v(30.04, 75.53) * mm, "end": v(29.13, 75.9) * mm});
            skArc(sketch, "E11.28.5", {"start": v(30.5, 74.98) * mm, "mid": v(30.34, 75.31) * mm, "end": v(30.04, 75.53) * mm});
            skArc(sketch, "E11.28.6", {"start": v(31, 69.61) * mm, "mid": v(30.94, 72.31) * mm, "end": v(30.5, 74.98) * mm});
            skArc(sketch, "E11.28.7", {"start": v(29.44, 65.55) * mm, "mid": v(29.44, 64.98) * mm, "end": v(29.84, 64.56) * mm});
            skLineSegment(sketch, "E11.28.8", {"start": v(31, 69.61) * mm, "end": v(29.44, 65.55) * mm});
            skLineSegment(sketch, "E11.28.9", {"start": v(23.55, 72.47) * mm, "end": v(21.99, 68.41) * mm});
            skArc(sketch, "E11.29.0", {"start": v(6.44, 70.83) * mm, "mid": v(7, 71) * mm, "end": v(7.29, 71.49) * mm});
            skArc(sketch, "E11.29.1", {"start": v(7.97, 75.78) * mm, "mid": v(9.36, 78.1) * mm, "end": v(11.07, 80.19) * mm});
            skArc(sketch, "E11.29.2", {"start": v(11.75, 80.43) * mm, "mid": v(11.38, 80.4) * mm, "end": v(11.07, 80.19) * mm});
            skLineSegment(sketch, "E11.29.3", {"start": v(11.75, 80.43) * mm, "end": v(12.72, 80.3) * mm});
            skLineSegment(sketch, "E11.29.4", {"start": v(13.68, 80.12) * mm, "end": v(12.72, 80.3) * mm});
            skArc(sketch, "E11.29.5", {"start": v(14.25, 79.68) * mm, "mid": v(14.02, 79.97) * mm, "end": v(13.68, 80.12) * mm});
            skArc(sketch, "E11.29.6", {"start": v(15.84, 74.53) * mm, "mid": v(15.23, 77.17) * mm, "end": v(14.25, 79.68) * mm});
            skArc(sketch, "E11.29.7", {"start": v(15.16, 70.24) * mm, "mid": v(15.29, 69.68) * mm, "end": v(15.77, 69.35) * mm});
            skLineSegment(sketch, "E11.29.8", {"start": v(15.84, 74.53) * mm, "end": v(15.16, 70.24) * mm});
            skLineSegment(sketch, "E11.29.9", {"start": v(7.97, 75.78) * mm, "end": v(7.29, 71.49) * mm});
            skArc(sketch, "E12.trimOffspring", {"start": v(-22.93, 67.32) * mm, "mid": v(-25.49, 66.4) * mm, "end": v(-28, 65.37) * mm});
            skArc(sketch, "E13.trimOffspring", {"start": v(6.44, 70.83) * mm, "mid": v(3.72, 71.02) * mm, "end": v(1, 71.11) * mm});
            skArc(sketch, "E14.trimOffspring", {"start": v(21.02, 67.94) * mm, "mid": v(18.4, 68.7) * mm, "end": v(15.77, 69.35) * mm});
            skArc(sketch, "E15.trimOffspring", {"start": v(34.69, 62.09) * mm, "mid": v(32.29, 63.37) * mm, "end": v(29.84, 64.56) * mm});
            skArc(sketch, "E16.trimOffspring", {"start": v(46.84, 53.52) * mm, "mid": v(44.76, 55.27) * mm, "end": v(42.61, 56.94) * mm});
            skArc(sketch, "E17.trimOffspring", {"start": v(56.94, 42.61) * mm, "mid": v(55.27, 44.76) * mm, "end": v(53.52, 46.84) * mm});
            skArc(sketch, "E18.trimOffspring", {"start": v(64.56, 29.84) * mm, "mid": v(63.37, 32.29) * mm, "end": v(62.09, 34.69) * mm});
            skArc(sketch, "E19.trimOffspring", {"start": v(69.35, 15.77) * mm, "mid": v(68.7, 18.4) * mm, "end": v(67.94, 21.02) * mm});
            skArc(sketch, "E20.trimOffspring", {"start": v(71.11, 1) * mm, "mid": v(71.02, 3.72) * mm, "end": v(70.83, 6.44) * mm});
            skArc(sketch, "E21.trimOffspring", {"start": v(69.77, -13.8) * mm, "mid": v(70.24, -11.13) * mm, "end": v(70.62, -8.43) * mm});
            skArc(sketch, "E22.trimOffspring", {"start": v(65.37, -28) * mm, "mid": v(66.4, -25.49) * mm, "end": v(67.32, -22.93) * mm});
            skArc(sketch, "E23.trimOffspring", {"start": v(58.12, -40.99) * mm, "mid": v(59.65, -38.73) * mm, "end": v(61.08, -36.42) * mm});
            skArc(sketch, "E24.trimOffspring", {"start": v(48.33, -52.18) * mm, "mid": v(50.29, -50.29) * mm, "end": v(52.18, -48.33) * mm});
            skArc(sketch, "E25.trimOffspring", {"start": v(36.42, -61.08) * mm, "mid": v(38.73, -59.65) * mm, "end": v(40.99, -58.12) * mm});
            skArc(sketch, "E26.trimOffspring", {"start": v(22.93, -67.32) * mm, "mid": v(25.49, -66.4) * mm, "end": v(28, -65.37) * mm});
            skArc(sketch, "E27.trimOffspring", {"start": v(-6.44, -70.83) * mm, "mid": v(-3.72, -71.02) * mm, "end": v(-1, -71.11) * mm});
            skArc(sketch, "E28.trimOffspring", {"start": v(8.43, -70.62) * mm, "mid": v(11.13, -70.24) * mm, "end": v(13.8, -69.77) * mm});
            skArc(sketch, "E29.trimOffspring", {"start": v(-21.02, -67.94) * mm, "mid": v(-18.4, -68.7) * mm, "end": v(-15.77, -69.35) * mm});
            skArc(sketch, "E30.trimOffspring", {"start": v(-34.69, -62.09) * mm, "mid": v(-32.29, -63.37) * mm, "end": v(-29.84, -64.56) * mm});
            skArc(sketch, "E31.trimOffspring", {"start": v(-46.84, -53.52) * mm, "mid": v(-44.76, -55.27) * mm, "end": v(-42.61, -56.94) * mm});
            skArc(sketch, "E32.trimOffspring", {"start": v(-56.94, -42.61) * mm, "mid": v(-55.27, -44.76) * mm, "end": v(-53.52, -46.84) * mm});
            skArc(sketch, "E33.trimOffspring", {"start": v(-64.56, -29.84) * mm, "mid": v(-63.37, -32.29) * mm, "end": v(-62.09, -34.69) * mm});
            skArc(sketch, "E34.trimOffspring", {"start": v(-69.35, -15.77) * mm, "mid": v(-68.7, -18.4) * mm, "end": v(-67.94, -21.02) * mm});
            skArc(sketch, "E35.trimOffspring", {"start": v(-71.11, -1) * mm, "mid": v(-71.02, -3.72) * mm, "end": v(-70.83, -6.44) * mm});
            skArc(sketch, "E36.trimOffspring", {"start": v(-69.77, 13.8) * mm, "mid": v(-70.24, 11.13) * mm, "end": v(-70.62, 8.43) * mm});
            skArc(sketch, "E37.trimOffspring", {"start": v(-65.37, 28) * mm, "mid": v(-66.4, 25.49) * mm, "end": v(-67.32, 22.93) * mm});
            skArc(sketch, "E38.trimOffspring", {"start": v(-58.12, 40.99) * mm, "mid": v(-59.65, 38.73) * mm, "end": v(-61.08, 36.42) * mm});
            skArc(sketch, "E39.trimOffspring", {"start": v(-48.33, 52.18) * mm, "mid": v(-50.29, 50.29) * mm, "end": v(-52.18, 48.33) * mm});
            skArc(sketch, "E40.trimOffspring", {"start": v(-36.42, 61.08) * mm, "mid": v(-38.73, 59.65) * mm, "end": v(-40.99, 58.12) * mm});
            skArc(sketch, "E41", {"start": v(-4.89, 65.86) * mm, "mid": v(-6.21, 65.75) * mm, "end": v(-7.54, 65.6) * mm});
            skLineSegment(sketch, "E42.MirrorCS", {"start": v(-3.99, 63.37) * mm, "end": v(-4.04, 65.1) * mm});
            skArc(sketch, "E43.MirrorCS", {"start": v(-3.99, 63.37) * mm, "mid": v(-3.53, 62.3) * mm, "end": v(-2.99, 61.25) * mm});
            skLineSegment(sketch, "E44.MirrorCS", {"start": v(-2.29, 60.85) * mm, "end": v(-1.91, 60.86) * mm});
            skLineSegment(sketch, "E45.MirrorCS", {"start": v(-1.54, 60.88) * mm, "end": v(-1.91, 60.86) * mm});
            skArc(sketch, "E46.MirrorCS", {"start": v(0, 63.5) * mm, "mid": v(-0.4, 62.4) * mm, "end": v(-0.87, 61.32) * mm});
            skLineSegment(sketch, "E47.MirrorCS", {"start": v(0, 63.5) * mm, "end": v(-0.05, 65.22) * mm});
            skPoint(sketch, "E48.visualSharp", {"position": v(-4.07, 65.91) * mm});
            skArc(sketch, "E48.filletArc", {"start": v(-4.04, 65.1) * mm, "mid": v(-4.3, 65.66) * mm, "end": v(-4.89, 65.86) * mm});
            skPoint(sketch, "E49.visualSharp", {"position": v(-0.08, 66.04) * mm});
            skArc(sketch, "E49.filletArc", {"start": v(0.74, 66.04) * mm, "mid": v(0.17, 65.8) * mm, "end": v(-0.05, 65.22) * mm});
            skPoint(sketch, "E50.visualSharp", {"position": v(-2.75, 60.84) * mm});
            skArc(sketch, "E50.filletArc", {"start": v(-2.99, 61.25) * mm, "mid": v(-2.7, 60.96) * mm, "end": v(-2.29, 60.85) * mm});
            skPoint(sketch, "E51.visualSharp", {"position": v(-1.08, 60.9) * mm});
            skArc(sketch, "E51.filletArc", {"start": v(-1.54, 60.88) * mm, "mid": v(-1.14, 61) * mm, "end": v(-0.87, 61.32) * mm});
            skLineSegment(sketch, "E52.1.0", {"start": v(-11.9, 62.37) * mm, "end": v(-12.17, 64.08) * mm});
            skArc(sketch, "E52.1.1", {"start": v(-11.9, 62.37) * mm, "mid": v(-11.3, 61.36) * mm, "end": v(-10.64, 60.4) * mm});
            skArc(sketch, "E52.1.2", {"start": v(-7.96, 63) * mm, "mid": v(-8.2, 61.85) * mm, "end": v(-8.54, 60.73) * mm});
            skLineSegment(sketch, "E52.1.3", {"start": v(-7.96, 63) * mm, "end": v(-8.23, 64.7) * mm});
            skArc(sketch, "E52.1.4", {"start": v(-9.16, 60.2) * mm, "mid": v(-8.78, 60.38) * mm, "end": v(-8.54, 60.73) * mm});
            skLineSegment(sketch, "E52.1.5", {"start": v(-9.16, 60.2) * mm, "end": v(-9.53, 60.14) * mm});
            skLineSegment(sketch, "E52.1.6", {"start": v(-9.9, 60.09) * mm, "end": v(-9.53, 60.14) * mm});
            skArc(sketch, "E52.1.7", {"start": v(-10.64, 60.4) * mm, "mid": v(-10.3, 60.14) * mm, "end": v(-9.9, 60.09) * mm});
            skArc(sketch, "E52.1.8", {"start": v(-7.54, 65.6) * mm, "mid": v(-8.08, 65.3) * mm, "end": v(-8.23, 64.7) * mm});
            skArc(sketch, "E52.1.9", {"start": v(-12.17, 64.08) * mm, "mid": v(-12.5, 64.6) * mm, "end": v(-13.1, 64.73) * mm});
            skLineSegment(sketch, "E52.2.0", {"start": v(-19.62, 60.39) * mm, "end": v(-20.1, 62.05) * mm});
            skArc(sketch, "E52.2.1", {"start": v(-19.62, 60.39) * mm, "mid": v(-18.9, 59.46) * mm, "end": v(-18.13, 58.58) * mm});
            skArc(sketch, "E52.2.2", {"start": v(-15.8, 61.5) * mm, "mid": v(-15.9, 60.33) * mm, "end": v(-16.09, 59.18) * mm});
            skLineSegment(sketch, "E52.2.3", {"start": v(-15.8, 61.5) * mm, "end": v(-16.27, 63.16) * mm});
            skArc(sketch, "E52.2.4", {"start": v(-16.63, 58.58) * mm, "mid": v(-16.28, 58.8) * mm, "end": v(-16.09, 59.18) * mm});
            skLineSegment(sketch, "E52.2.5", {"start": v(-16.63, 58.58) * mm, "end": v(-16.99, 58.47) * mm});
            skLineSegment(sketch, "E52.2.6", {"start": v(-17.35, 58.37) * mm, "end": v(-16.99, 58.47) * mm});
            skArc(sketch, "E52.2.7", {"start": v(-18.13, 58.58) * mm, "mid": v(-17.77, 58.37) * mm, "end": v(-17.35, 58.37) * mm});
            skArc(sketch, "E52.2.8", {"start": v(-15.7, 64.15) * mm, "mid": v(-16.2, 63.77) * mm, "end": v(-16.27, 63.16) * mm});
            skArc(sketch, "E52.2.9", {"start": v(-20.1, 62.05) * mm, "mid": v(-20.5, 62.53) * mm, "end": v(-21.11, 62.57) * mm});
            skLineSegment(sketch, "E52.3.0", {"start": v(-27.04, 57.45) * mm, "end": v(-27.72, 59.04) * mm});
            skArc(sketch, "E52.3.1", {"start": v(-27.04, 57.45) * mm, "mid": v(-26.2, 56.62) * mm, "end": v(-25.32, 55.85) * mm});
            skArc(sketch, "E52.3.2", {"start": v(-23.37, 59.04) * mm, "mid": v(-23.33, 57.87) * mm, "end": v(-23.38, 56.7) * mm});
            skLineSegment(sketch, "E52.3.3", {"start": v(-23.37, 59.04) * mm, "end": v(-24.06, 60.62) * mm});
            skArc(sketch, "E52.3.4", {"start": v(-23.84, 56.03) * mm, "mid": v(-23.52, 56.3) * mm, "end": v(-23.38, 56.7) * mm});
            skLineSegment(sketch, "E52.3.5", {"start": v(-23.84, 56.03) * mm, "end": v(-24.18, 55.88) * mm});
            skLineSegment(sketch, "E52.3.6", {"start": v(-24.53, 55.74) * mm, "end": v(-24.18, 55.88) * mm});
            skArc(sketch, "E52.3.7", {"start": v(-25.32, 55.85) * mm, "mid": v(-24.94, 55.68) * mm, "end": v(-24.53, 55.74) * mm});
            skArc(sketch, "E52.3.8", {"start": v(-23.62, 61.67) * mm, "mid": v(-24.06, 61.24) * mm, "end": v(-24.06, 60.62) * mm});
            skArc(sketch, "E52.3.9", {"start": v(-27.72, 59.04) * mm, "mid": v(-28.17, 59.46) * mm, "end": v(-28.79, 59.44) * mm});
            skLineSegment(sketch, "E52.4.0", {"start": v(-34.02, 53.61) * mm, "end": v(-34.9, 55.1) * mm});
            skArc(sketch, "E52.4.1", {"start": v(-34.02, 53.61) * mm, "mid": v(-33.1, 52.89) * mm, "end": v(-32.12, 52.24) * mm});
            skArc(sketch, "E52.4.2", {"start": v(-30.59, 55.64) * mm, "mid": v(-30.4, 54.49) * mm, "end": v(-30.3, 53.32) * mm});
            skLineSegment(sketch, "E52.4.3", {"start": v(-30.59, 55.64) * mm, "end": v(-31.47, 57.13) * mm});
            skArc(sketch, "E52.4.4", {"start": v(-30.68, 52.6) * mm, "mid": v(-30.39, 52.9) * mm, "end": v(-30.3, 53.32) * mm});
            skLineSegment(sketch, "E52.4.5", {"start": v(-30.68, 52.6) * mm, "end": v(-31, 52.4) * mm});
            skLineSegment(sketch, "E52.4.6", {"start": v(-31.32, 52.22) * mm, "end": v(-31, 52.4) * mm});
            skArc(sketch, "E52.4.7", {"start": v(-32.12, 52.24) * mm, "mid": v(-31.72, 52.12) * mm, "end": v(-31.32, 52.22) * mm});
            skArc(sketch, "E52.4.8", {"start": v(-31.16, 58.22) * mm, "mid": v(-31.55, 57.74) * mm, "end": v(-31.47, 57.13) * mm});
            skArc(sketch, "E52.4.9", {"start": v(-34.9, 55.1) * mm, "mid": v(-35.4, 55.47) * mm, "end": v(-36, 55.36) * mm});
            skLineSegment(sketch, "E52.5.0", {"start": v(-40.47, 48.93) * mm, "end": v(-41.53, 50.3) * mm});
            skArc(sketch, "E52.5.1", {"start": v(-40.47, 48.93) * mm, "mid": v(-39.47, 48.32) * mm, "end": v(-38.42, 47.8) * mm});
            skArc(sketch, "E52.5.2", {"start": v(-37.32, 51.37) * mm, "mid": v(-37, 50.25) * mm, "end": v(-36.74, 49.1) * mm});
            skLineSegment(sketch, "E52.5.3", {"start": v(-37.32, 51.37) * mm, "end": v(-38.38, 52.74) * mm});
            skArc(sketch, "E52.5.4", {"start": v(-37.03, 48.34) * mm, "mid": v(-36.78, 48.68) * mm, "end": v(-36.74, 49.1) * mm});
            skLineSegment(sketch, "E52.5.5", {"start": v(-37.03, 48.34) * mm, "end": v(-37.32, 48.11) * mm});
            skLineSegment(sketch, "E52.5.6", {"start": v(-37.62, 47.89) * mm, "end": v(-37.32, 48.11) * mm});
            skArc(sketch, "E52.5.7", {"start": v(-38.42, 47.8) * mm, "mid": v(-38, 47.73) * mm, "end": v(-37.62, 47.89) * mm});
            skArc(sketch, "E52.5.8", {"start": v(-38.21, 53.86) * mm, "mid": v(-38.54, 53.33) * mm, "end": v(-38.38, 52.74) * mm});
            skArc(sketch, "E52.5.9", {"start": v(-41.53, 50.3) * mm, "mid": v(-42.07, 50.6) * mm, "end": v(-42.66, 50.4) * mm});
            skLineSegment(sketch, "E52.6.0", {"start": v(-46.29, 43.47) * mm, "end": v(-47.5, 44.69) * mm});
            skArc(sketch, "E52.6.1", {"start": v(-46.29, 43.47) * mm, "mid": v(-45.21, 43) * mm, "end": v(-44.1, 42.6) * mm});
            skArc(sketch, "E52.6.2", {"start": v(-43.47, 46.29) * mm, "mid": v(-43, 45.21) * mm, "end": v(-42.6, 44.1) * mm});
            skLineSegment(sketch, "E52.6.3", {"start": v(-43.47, 46.29) * mm, "end": v(-44.69, 47.5) * mm});
            skArc(sketch, "E52.6.4", {"start": v(-42.8, 43.32) * mm, "mid": v(-42.6, 43.69) * mm, "end": v(-42.6, 44.1) * mm});
            skLineSegment(sketch, "E52.6.5", {"start": v(-42.8, 43.32) * mm, "end": v(-43.06, 43.06) * mm});
            skLineSegment(sketch, "E52.6.6", {"start": v(-43.32, 42.8) * mm, "end": v(-43.06, 43.06) * mm});
            skArc(sketch, "E52.6.7", {"start": v(-44.1, 42.6) * mm, "mid": v(-43.69, 42.6) * mm, "end": v(-43.32, 42.8) * mm});
            skArc(sketch, "E52.6.8", {"start": v(-44.66, 48.65) * mm, "mid": v(-44.92, 48.08) * mm, "end": v(-44.69, 47.5) * mm});
            skArc(sketch, "E52.6.9", {"start": v(-47.5, 44.69) * mm, "mid": v(-48.08, 44.92) * mm, "end": v(-48.65, 44.66) * mm});
            skLineSegment(sketch, "E52.7.0", {"start": v(-51.37, 37.32) * mm, "end": v(-52.74, 38.38) * mm});
            skArc(sketch, "E52.7.1", {"start": v(-51.37, 37.32) * mm, "mid": v(-50.25, 37) * mm, "end": v(-49.1, 36.74) * mm});
            skArc(sketch, "E52.7.2", {"start": v(-48.93, 40.47) * mm, "mid": v(-48.32, 39.47) * mm, "end": v(-47.8, 38.42) * mm});
            skLineSegment(sketch, "E52.7.3", {"start": v(-48.93, 40.47) * mm, "end": v(-50.3, 41.53) * mm});
            skArc(sketch, "E52.7.4", {"start": v(-47.89, 37.62) * mm, "mid": v(-47.73, 38) * mm, "end": v(-47.8, 38.42) * mm});
            skLineSegment(sketch, "E52.7.5", {"start": v(-47.89, 37.62) * mm, "end": v(-48.11, 37.32) * mm});
            skLineSegment(sketch, "E52.7.6", {"start": v(-48.34, 37.03) * mm, "end": v(-48.11, 37.32) * mm});
            skArc(sketch, "E52.7.7", {"start": v(-49.1, 36.74) * mm, "mid": v(-48.68, 36.78) * mm, "end": v(-48.34, 37.03) * mm});
            skArc(sketch, "E52.7.8", {"start": v(-50.4, 42.66) * mm, "mid": v(-50.6, 42.07) * mm, "end": v(-50.3, 41.53) * mm});
            skArc(sketch, "E52.7.9", {"start": v(-52.74, 38.38) * mm, "mid": v(-53.33, 38.54) * mm, "end": v(-53.86, 38.21) * mm});
            skLineSegment(sketch, "E52.8.0", {"start": v(-55.64, 30.59) * mm, "end": v(-57.13, 31.47) * mm});
            skArc(sketch, "E52.8.1", {"start": v(-55.64, 30.59) * mm, "mid": v(-54.49, 30.4) * mm, "end": v(-53.32, 30.3) * mm});
            skArc(sketch, "E52.8.2", {"start": v(-53.61, 34.02) * mm, "mid": v(-52.89, 33.1) * mm, "end": v(-52.24, 32.12) * mm});
            skLineSegment(sketch, "E52.8.3", {"start": v(-53.61, 34.02) * mm, "end": v(-55.1, 34.9) * mm});
            skArc(sketch, "E52.8.4", {"start": v(-52.22, 31.32) * mm, "mid": v(-52.12, 31.72) * mm, "end": v(-52.24, 32.12) * mm});
            skLineSegment(sketch, "E52.8.5", {"start": v(-52.22, 31.32) * mm, "end": v(-52.4, 31) * mm});
            skLineSegment(sketch, "E52.8.6", {"start": v(-52.6, 30.68) * mm, "end": v(-52.4, 31) * mm});
            skArc(sketch, "E52.8.7", {"start": v(-53.32, 30.3) * mm, "mid": v(-52.9, 30.39) * mm, "end": v(-52.6, 30.68) * mm});
            skArc(sketch, "E52.8.8", {"start": v(-55.36, 36) * mm, "mid": v(-55.47, 35.4) * mm, "end": v(-55.1, 34.9) * mm});
            skArc(sketch, "E52.8.9", {"start": v(-57.13, 31.47) * mm, "mid": v(-57.74, 31.55) * mm, "end": v(-58.22, 31.16) * mm});
            skLineSegment(sketch, "E52.9.0", {"start": v(-59.04, 23.37) * mm, "end": v(-60.62, 24.06) * mm});
            skArc(sketch, "E52.9.1", {"start": v(-59.04, 23.37) * mm, "mid": v(-57.87, 23.33) * mm, "end": v(-56.7, 23.38) * mm});
            skArc(sketch, "E52.9.2", {"start": v(-57.45, 27.04) * mm, "mid": v(-56.62, 26.2) * mm, "end": v(-55.85, 25.32) * mm});
            skLineSegment(sketch, "E52.9.3", {"start": v(-57.45, 27.04) * mm, "end": v(-59.04, 27.72) * mm});
            skArc(sketch, "E52.9.4", {"start": v(-55.74, 24.53) * mm, "mid": v(-55.68, 24.94) * mm, "end": v(-55.85, 25.32) * mm});
            skLineSegment(sketch, "E52.9.5", {"start": v(-55.74, 24.53) * mm, "end": v(-55.88, 24.18) * mm});
            skLineSegment(sketch, "E52.9.6", {"start": v(-56.03, 23.84) * mm, "end": v(-55.88, 24.18) * mm});
            skArc(sketch, "E52.9.7", {"start": v(-56.7, 23.38) * mm, "mid": v(-56.3, 23.52) * mm, "end": v(-56.03, 23.84) * mm});
            skArc(sketch, "E52.9.8", {"start": v(-59.44, 28.79) * mm, "mid": v(-59.46, 28.17) * mm, "end": v(-59.04, 27.72) * mm});
            skArc(sketch, "E52.9.9", {"start": v(-60.62, 24.06) * mm, "mid": v(-61.24, 24.06) * mm, "end": v(-61.67, 23.62) * mm});
            skLineSegment(sketch, "E52.10.0", {"start": v(-61.5, 15.8) * mm, "end": v(-63.16, 16.27) * mm});
            skArc(sketch, "E52.10.1", {"start": v(-61.5, 15.8) * mm, "mid": v(-60.33, 15.9) * mm, "end": v(-59.18, 16.09) * mm});
            skArc(sketch, "E52.10.2", {"start": v(-60.39, 19.62) * mm, "mid": v(-59.46, 18.9) * mm, "end": v(-58.58, 18.13) * mm});
            skLineSegment(sketch, "E52.10.3", {"start": v(-60.39, 19.62) * mm, "end": v(-62.05, 20.1) * mm});
            skArc(sketch, "E52.10.4", {"start": v(-58.37, 17.35) * mm, "mid": v(-58.37, 17.77) * mm, "end": v(-58.58, 18.13) * mm});
            skLineSegment(sketch, "E52.10.5", {"start": v(-58.37, 17.35) * mm, "end": v(-58.47, 16.99) * mm});
            skLineSegment(sketch, "E52.10.6", {"start": v(-58.58, 16.63) * mm, "end": v(-58.47, 16.99) * mm});
            skArc(sketch, "E52.10.7", {"start": v(-59.18, 16.09) * mm, "mid": v(-58.8, 16.28) * mm, "end": v(-58.58, 16.63) * mm});
            skArc(sketch, "E52.10.8", {"start": v(-62.57, 21.11) * mm, "mid": v(-62.53, 20.5) * mm, "end": v(-62.05, 20.1) * mm});
            skArc(sketch, "E52.10.9", {"start": v(-63.16, 16.27) * mm, "mid": v(-63.77, 16.2) * mm, "end": v(-64.15, 15.7) * mm});
            skLineSegment(sketch, "E52.11.0", {"start": v(-63, 7.96) * mm, "end": v(-64.7, 8.23) * mm});
            skArc(sketch, "E52.11.1", {"start": v(-63, 7.96) * mm, "mid": v(-61.85, 8.2) * mm, "end": v(-60.73, 8.54) * mm});
            skArc(sketch, "E52.11.2", {"start": v(-62.37, 11.9) * mm, "mid": v(-61.36, 11.3) * mm, "end": v(-60.4, 10.64) * mm});
            skLineSegment(sketch, "E52.11.3", {"start": v(-62.37, 11.9) * mm, "end": v(-64.08, 12.17) * mm});
            skArc(sketch, "E52.11.4", {"start": v(-60.09, 9.9) * mm, "mid": v(-60.14, 10.3) * mm, "end": v(-60.4, 10.64) * mm});
            skLineSegment(sketch, "E52.11.5", {"start": v(-60.09, 9.9) * mm, "end": v(-60.14, 9.53) * mm});
            skLineSegment(sketch, "E52.11.6", {"start": v(-60.2, 9.16) * mm, "end": v(-60.14, 9.53) * mm});
            skArc(sketch, "E52.11.7", {"start": v(-60.73, 8.54) * mm, "mid": v(-60.38, 8.78) * mm, "end": v(-60.2, 9.16) * mm});
            skArc(sketch, "E52.11.8", {"start": v(-64.73, 13.1) * mm, "mid": v(-64.6, 12.5) * mm, "end": v(-64.08, 12.17) * mm});
            skArc(sketch, "E52.11.9", {"start": v(-64.7, 8.23) * mm, "mid": v(-65.3, 8.08) * mm, "end": v(-65.6, 7.54) * mm});
            skLineSegment(sketch, "E52.12.0", {"start": v(-63.5, 0) * mm, "end": v(-65.22, 0.05) * mm});
            skArc(sketch, "E52.12.1", {"start": v(-63.5, 0) * mm, "mid": v(-62.4, 0.4) * mm, "end": v(-61.32, 0.87) * mm});
            skArc(sketch, "E52.12.2", {"start": v(-63.37, 3.99) * mm, "mid": v(-62.3, 3.53) * mm, "end": v(-61.25, 2.99) * mm});
            skLineSegment(sketch, "E52.12.3", {"start": v(-63.37, 3.99) * mm, "end": v(-65.1, 4.04) * mm});
            skArc(sketch, "E52.12.4", {"start": v(-60.85, 2.29) * mm, "mid": v(-60.96, 2.7) * mm, "end": v(-61.25, 2.99) * mm});
            skLineSegment(sketch, "E52.12.5", {"start": v(-60.85, 2.29) * mm, "end": v(-60.86, 1.91) * mm});
            skLineSegment(sketch, "E52.12.6", {"start": v(-60.88, 1.54) * mm, "end": v(-60.86, 1.91) * mm});
            skArc(sketch, "E52.12.7", {"start": v(-61.32, 0.87) * mm, "mid": v(-61, 1.14) * mm, "end": v(-60.88, 1.54) * mm});
            skArc(sketch, "E52.12.8", {"start": v(-65.86, 4.89) * mm, "mid": v(-65.66, 4.3) * mm, "end": v(-65.1, 4.04) * mm});
            skArc(sketch, "E52.12.9", {"start": v(-65.22, 0.05) * mm, "mid": v(-65.8, -0.17) * mm, "end": v(-66.04, -0.74) * mm});
            skLineSegment(sketch, "E52.13.0", {"start": v(-63, -7.96) * mm, "end": v(-64.72, -8.12) * mm});
            skArc(sketch, "E52.13.1", {"start": v(-63, -7.96) * mm, "mid": v(-61.95, -7.43) * mm, "end": v(-60.94, -6.83) * mm});
            skArc(sketch, "E52.13.2", {"start": v(-63.37, -3.99) * mm, "mid": v(-62.24, -4.3) * mm, "end": v(-61.14, -4.71) * mm});
            skLineSegment(sketch, "E52.13.3", {"start": v(-63.37, -3.99) * mm, "end": v(-65.1, -4.15) * mm});
            skArc(sketch, "E52.13.4", {"start": v(-60.66, -5.36) * mm, "mid": v(-60.81, -4.97) * mm, "end": v(-61.14, -4.71) * mm});
            skLineSegment(sketch, "E52.13.5", {"start": v(-60.66, -5.36) * mm, "end": v(-60.62, -5.73) * mm});
            skLineSegment(sketch, "E52.13.6", {"start": v(-60.59, -6.1) * mm, "end": v(-60.62, -5.73) * mm});
            skArc(sketch, "E52.13.7", {"start": v(-60.94, -6.83) * mm, "mid": v(-60.67, -6.51) * mm, "end": v(-60.59, -6.1) * mm});
            skArc(sketch, "E52.13.8", {"start": v(-65.95, -3.4) * mm, "mid": v(-65.68, -3.96) * mm, "end": v(-65.1, -4.15) * mm});
            skArc(sketch, "E52.13.9", {"start": v(-64.72, -8.12) * mm, "mid": v(-65.26, -8.42) * mm, "end": v(-65.42, -9.01) * mm});
            skLineSegment(sketch, "E52.14.0", {"start": v(-61.5, -15.8) * mm, "end": v(-63.19, -16.17) * mm});
            skArc(sketch, "E52.14.1", {"start": v(-61.5, -15.8) * mm, "mid": v(-60.53, -15.14) * mm, "end": v(-59.6, -14.41) * mm});
            skArc(sketch, "E52.14.2", {"start": v(-62.37, -11.9) * mm, "mid": v(-61.21, -12.08) * mm, "end": v(-60.07, -12.34) * mm});
            skLineSegment(sketch, "E52.14.3", {"start": v(-62.37, -11.9) * mm, "end": v(-64.06, -12.27) * mm});
            skArc(sketch, "E52.14.4", {"start": v(-59.5, -12.92) * mm, "mid": v(-59.7, -12.55) * mm, "end": v(-60.07, -12.34) * mm});
            skLineSegment(sketch, "E52.14.5", {"start": v(-59.5, -12.92) * mm, "end": v(-59.42, -13.28) * mm});
            skLineSegment(sketch, "E52.14.6", {"start": v(-59.35, -13.65) * mm, "end": v(-59.42, -13.28) * mm});
            skArc(sketch, "E52.14.7", {"start": v(-59.6, -14.41) * mm, "mid": v(-59.37, -14.07) * mm, "end": v(-59.35, -13.65) * mm});
            skArc(sketch, "E52.14.8", {"start": v(-65, -11.65) * mm, "mid": v(-64.67, -12.16) * mm, "end": v(-64.06, -12.27) * mm});
            skArc(sketch, "E52.14.9", {"start": v(-63.19, -16.17) * mm, "mid": v(-63.7, -16.53) * mm, "end": v(-63.78, -17.14) * mm});
            skLineSegment(sketch, "E52.15.0", {"start": v(-59.04, -23.37) * mm, "end": v(-60.66, -23.96) * mm});
            skArc(sketch, "E52.15.1", {"start": v(-59.04, -23.37) * mm, "mid": v(-58.15, -22.6) * mm, "end": v(-57.33, -21.77) * mm});
            skArc(sketch, "E52.15.2", {"start": v(-60.39, -19.62) * mm, "mid": v(-59.22, -19.65) * mm, "end": v(-58.05, -19.77) * mm});
            skLineSegment(sketch, "E52.15.3", {"start": v(-60.39, -19.62) * mm, "end": v(-62.01, -20.2) * mm});
            skArc(sketch, "E52.15.4", {"start": v(-57.42, -20.28) * mm, "mid": v(-57.67, -19.94) * mm, "end": v(-58.05, -19.77) * mm});
            skLineSegment(sketch, "E52.15.5", {"start": v(-57.42, -20.28) * mm, "end": v(-57.29, -20.63) * mm});
            skLineSegment(sketch, "E52.15.6", {"start": v(-57.17, -20.98) * mm, "end": v(-57.29, -20.63) * mm});
            skArc(sketch, "E52.15.7", {"start": v(-57.33, -21.77) * mm, "mid": v(-57.14, -21.4) * mm, "end": v(-57.17, -20.98) * mm});
            skArc(sketch, "E52.15.8", {"start": v(-63.03, -19.7) * mm, "mid": v(-62.63, -20.17) * mm, "end": v(-62.01, -20.2) * mm});
            skArc(sketch, "E52.15.9", {"start": v(-60.66, -23.96) * mm, "mid": v(-61.12, -24.38) * mm, "end": v(-61.13, -25) * mm});
            skLineSegment(sketch, "E52.16.0", {"start": v(-55.64, -30.6) * mm, "end": v(-57.18, -31.37) * mm});
            skArc(sketch, "E52.16.1", {"start": v(-55.64, -30.6) * mm, "mid": v(-54.86, -29.71) * mm, "end": v(-54.15, -28.78) * mm});
            skArc(sketch, "E52.16.2", {"start": v(-57.45, -27.04) * mm, "mid": v(-56.29, -26.92) * mm, "end": v(-55.11, -26.9) * mm});
            skLineSegment(sketch, "E52.16.3", {"start": v(-57.45, -27.04) * mm, "end": v(-59, -27.82) * mm});
            skArc(sketch, "E52.16.4", {"start": v(-54.43, -27.31) * mm, "mid": v(-54.71, -27) * mm, "end": v(-55.11, -26.9) * mm});
            skLineSegment(sketch, "E52.16.5", {"start": v(-54.43, -27.31) * mm, "end": v(-54.25, -27.64) * mm});
            skLineSegment(sketch, "E52.16.6", {"start": v(-54.09, -27.98) * mm, "end": v(-54.25, -27.64) * mm});
            skArc(sketch, "E52.16.7", {"start": v(-54.15, -28.78) * mm, "mid": v(-54, -28.39) * mm, "end": v(-54.09, -27.98) * mm});
            skArc(sketch, "E52.16.8", {"start": v(-60.07, -27.45) * mm, "mid": v(-59.6, -27.86) * mm, "end": v(-59, -27.82) * mm});
            skArc(sketch, "E52.16.9", {"start": v(-57.18, -31.37) * mm, "mid": v(-57.58, -31.85) * mm, "end": v(-57.51, -32.46) * mm});
            skLineSegment(sketch, "E52.17.0", {"start": v(-51.37, -37.32) * mm, "end": v(-52.8, -38.3) * mm});
            skArc(sketch, "E52.17.1", {"start": v(-51.37, -37.32) * mm, "mid": v(-50.7, -36.36) * mm, "end": v(-50.12, -35.34) * mm});
            skArc(sketch, "E52.17.2", {"start": v(-53.61, -34.02) * mm, "mid": v(-52.47, -33.76) * mm, "end": v(-51.3, -33.59) * mm});
            skLineSegment(sketch, "E52.17.3", {"start": v(-53.61, -34.02) * mm, "end": v(-55.04, -35) * mm});
            skArc(sketch, "E52.17.4", {"start": v(-50.57, -33.92) * mm, "mid": v(-50.9, -33.65) * mm, "end": v(-51.3, -33.59) * mm});
            skLineSegment(sketch, "E52.17.5", {"start": v(-50.57, -33.92) * mm, "end": v(-50.36, -34.22) * mm});
            skLineSegment(sketch, "E52.17.6", {"start": v(-50.15, -34.54) * mm, "end": v(-50.36, -34.22) * mm});
            skArc(sketch, "E52.17.7", {"start": v(-50.12, -35.34) * mm, "mid": v(-50.02, -34.93) * mm, "end": v(-50.15, -34.54) * mm});
            skArc(sketch, "E52.17.8", {"start": v(-56.15, -34.76) * mm, "mid": v(-55.65, -35.11) * mm, "end": v(-55.04, -35) * mm});
            skArc(sketch, "E52.17.9", {"start": v(-52.8, -38.3) * mm, "mid": v(-53.13, -38.81) * mm, "end": v(-52.99, -39.41) * mm});
            skLineSegment(sketch, "E52.18.0", {"start": v(-46.29, -43.47) * mm, "end": v(-47.58, -44.6) * mm});
            skArc(sketch, "E52.18.1", {"start": v(-46.29, -43.47) * mm, "mid": v(-45.75, -42.42) * mm, "end": v(-45.3, -41.34) * mm});
            skArc(sketch, "E52.18.2", {"start": v(-48.93, -40.47) * mm, "mid": v(-47.82, -40.07) * mm, "end": v(-46.7, -39.75) * mm});
            skLineSegment(sketch, "E52.18.3", {"start": v(-48.93, -40.47) * mm, "end": v(-50.22, -41.62) * mm});
            skArc(sketch, "E52.18.4", {"start": v(-45.92, -39.99) * mm, "mid": v(-46.28, -39.77) * mm, "end": v(-46.7, -39.75) * mm});
            skLineSegment(sketch, "E52.18.5", {"start": v(-45.92, -39.99) * mm, "end": v(-45.67, -40.27) * mm});
            skLineSegment(sketch, "E52.18.6", {"start": v(-45.43, -40.55) * mm, "end": v(-45.67, -40.27) * mm});
            skArc(sketch, "E52.18.7", {"start": v(-45.3, -41.34) * mm, "mid": v(-45.25, -40.93) * mm, "end": v(-45.43, -40.55) * mm});
            skArc(sketch, "E52.18.8", {"start": v(-51.35, -41.52) * mm, "mid": v(-50.8, -41.81) * mm, "end": v(-50.22, -41.62) * mm});
            skArc(sketch, "E52.18.9", {"start": v(-47.58, -44.6) * mm, "mid": v(-47.85, -45.17) * mm, "end": v(-47.63, -45.75) * mm});
            skLineSegment(sketch, "E52.19.0", {"start": v(-40.47, -48.93) * mm, "end": v(-41.62, -50.22) * mm});
            skArc(sketch, "E52.19.1", {"start": v(-40.47, -48.93) * mm, "mid": v(-40.07, -47.82) * mm, "end": v(-39.75, -46.7) * mm});
            skArc(sketch, "E52.19.2", {"start": v(-43.47, -46.29) * mm, "mid": v(-42.42, -45.75) * mm, "end": v(-41.34, -45.3) * mm});
            skLineSegment(sketch, "E52.19.3", {"start": v(-43.47, -46.29) * mm, "end": v(-44.6, -47.58) * mm});
            skArc(sketch, "E52.19.4", {"start": v(-40.55, -45.43) * mm, "mid": v(-40.93, -45.25) * mm, "end": v(-41.34, -45.3) * mm});
            skLineSegment(sketch, "E52.19.5", {"start": v(-40.55, -45.43) * mm, "end": v(-40.27, -45.67) * mm});
            skLineSegment(sketch, "E52.19.6", {"start": v(-39.99, -45.92) * mm, "end": v(-40.27, -45.67) * mm});
            skArc(sketch, "E52.19.7", {"start": v(-39.75, -46.7) * mm, "mid": v(-39.77, -46.28) * mm, "end": v(-39.99, -45.92) * mm});
            skArc(sketch, "E52.19.8", {"start": v(-45.75, -47.63) * mm, "mid": v(-45.17, -47.85) * mm, "end": v(-44.6, -47.58) * mm});
            skArc(sketch, "E52.19.9", {"start": v(-41.62, -50.22) * mm, "mid": v(-41.81, -50.8) * mm, "end": v(-41.52, -51.35) * mm});
            skLineSegment(sketch, "E52.20.0", {"start": v(-34.02, -53.61) * mm, "end": v(-35, -55.04) * mm});
            skArc(sketch, "E52.20.1", {"start": v(-34.02, -53.61) * mm, "mid": v(-33.76, -52.47) * mm, "end": v(-33.59, -51.3) * mm});
            skArc(sketch, "E52.20.2", {"start": v(-37.32, -51.37) * mm, "mid": v(-36.36, -50.7) * mm, "end": v(-35.34, -50.12) * mm});
            skLineSegment(sketch, "E52.20.3", {"start": v(-37.32, -51.37) * mm, "end": v(-38.3, -52.8) * mm});
            skArc(sketch, "E52.20.4", {"start": v(-34.54, -50.15) * mm, "mid": v(-34.93, -50.02) * mm, "end": v(-35.34, -50.12) * mm});
            skLineSegment(sketch, "E52.20.5", {"start": v(-34.54, -50.15) * mm, "end": v(-34.22, -50.36) * mm});
            skLineSegment(sketch, "E52.20.6", {"start": v(-33.92, -50.57) * mm, "end": v(-34.22, -50.36) * mm});
            skArc(sketch, "E52.20.7", {"start": v(-33.59, -51.3) * mm, "mid": v(-33.65, -50.9) * mm, "end": v(-33.92, -50.57) * mm});
            skArc(sketch, "E52.20.8", {"start": v(-39.41, -52.99) * mm, "mid": v(-38.81, -53.13) * mm, "end": v(-38.3, -52.8) * mm});
            skArc(sketch, "E52.20.9", {"start": v(-35, -55.04) * mm, "mid": v(-35.11, -55.65) * mm, "end": v(-34.76, -56.15) * mm});
            skLineSegment(sketch, "E52.21.0", {"start": v(-27.04, -57.45) * mm, "end": v(-27.82, -59) * mm});
            skArc(sketch, "E52.21.1", {"start": v(-27.04, -57.45) * mm, "mid": v(-26.92, -56.29) * mm, "end": v(-26.9, -55.11) * mm});
            skArc(sketch, "E52.21.2", {"start": v(-30.6, -55.64) * mm, "mid": v(-29.71, -54.86) * mm, "end": v(-28.78, -54.15) * mm});
            skLineSegment(sketch, "E52.21.3", {"start": v(-30.6, -55.64) * mm, "end": v(-31.37, -57.18) * mm});
            skArc(sketch, "E52.21.4", {"start": v(-27.98, -54.09) * mm, "mid": v(-28.39, -54) * mm, "end": v(-28.78, -54.15) * mm});
            skLineSegment(sketch, "E52.21.5", {"start": v(-27.98, -54.09) * mm, "end": v(-27.64, -54.25) * mm});
            skLineSegment(sketch, "E52.21.6", {"start": v(-27.31, -54.43) * mm, "end": v(-27.64, -54.25) * mm});
            skArc(sketch, "E52.21.7", {"start": v(-26.9, -55.11) * mm, "mid": v(-27, -54.71) * mm, "end": v(-27.31, -54.43) * mm});
            skArc(sketch, "E52.21.8", {"start": v(-32.46, -57.51) * mm, "mid": v(-31.85, -57.58) * mm, "end": v(-31.37, -57.18) * mm});
            skArc(sketch, "E52.21.9", {"start": v(-27.82, -59) * mm, "mid": v(-27.86, -59.6) * mm, "end": v(-27.45, -60.07) * mm});
            skLineSegment(sketch, "E52.22.0", {"start": v(-19.62, -60.39) * mm, "end": v(-20.2, -62.01) * mm});
            skArc(sketch, "E52.22.1", {"start": v(-19.62, -60.39) * mm, "mid": v(-19.65, -59.22) * mm, "end": v(-19.77, -58.05) * mm});
            skArc(sketch, "E52.22.2", {"start": v(-23.37, -59.04) * mm, "mid": v(-22.6, -58.15) * mm, "end": v(-21.77, -57.33) * mm});
            skLineSegment(sketch, "E52.22.3", {"start": v(-23.37, -59.04) * mm, "end": v(-23.96, -60.66) * mm});
            skArc(sketch, "E52.22.4", {"start": v(-20.98, -57.17) * mm, "mid": v(-21.4, -57.14) * mm, "end": v(-21.77, -57.33) * mm});
            skLineSegment(sketch, "E52.22.5", {"start": v(-20.98, -57.17) * mm, "end": v(-20.63, -57.29) * mm});
            skLineSegment(sketch, "E52.22.6", {"start": v(-20.28, -57.42) * mm, "end": v(-20.63, -57.29) * mm});
            skArc(sketch, "E52.22.7", {"start": v(-19.77, -58.05) * mm, "mid": v(-19.94, -57.67) * mm, "end": v(-20.28, -57.42) * mm});
            skArc(sketch, "E52.22.8", {"start": v(-25, -61.13) * mm, "mid": v(-24.38, -61.12) * mm, "end": v(-23.96, -60.66) * mm});
            skArc(sketch, "E52.22.9", {"start": v(-20.2, -62.01) * mm, "mid": v(-20.17, -62.63) * mm, "end": v(-19.7, -63.03) * mm});
            skLineSegment(sketch, "E52.23.0", {"start": v(-11.9, -62.37) * mm, "end": v(-12.27, -64.06) * mm});
            skArc(sketch, "E52.23.1", {"start": v(-11.9, -62.37) * mm, "mid": v(-12.08, -61.21) * mm, "end": v(-12.34, -60.07) * mm});
            skArc(sketch, "E52.23.2", {"start": v(-15.8, -61.5) * mm, "mid": v(-15.14, -60.53) * mm, "end": v(-14.41, -59.6) * mm});
            skLineSegment(sketch, "E52.23.3", {"start": v(-15.8, -61.5) * mm, "end": v(-16.17, -63.19) * mm});
            skArc(sketch, "E52.23.4", {"start": v(-13.65, -59.35) * mm, "mid": v(-14.07, -59.37) * mm, "end": v(-14.41, -59.6) * mm});
            skLineSegment(sketch, "E52.23.5", {"start": v(-13.65, -59.35) * mm, "end": v(-13.28, -59.42) * mm});
            skLineSegment(sketch, "E52.23.6", {"start": v(-12.92, -59.5) * mm, "end": v(-13.28, -59.42) * mm});
            skArc(sketch, "E52.23.7", {"start": v(-12.34, -60.07) * mm, "mid": v(-12.55, -59.7) * mm, "end": v(-12.92, -59.5) * mm});
            skArc(sketch, "E52.23.8", {"start": v(-17.14, -63.78) * mm, "mid": v(-16.53, -63.7) * mm, "end": v(-16.17, -63.19) * mm});
            skArc(sketch, "E52.23.9", {"start": v(-12.27, -64.06) * mm, "mid": v(-12.16, -64.67) * mm, "end": v(-11.65, -65) * mm});
            skLineSegment(sketch, "E52.24.0", {"start": v(-3.99, -63.37) * mm, "end": v(-4.15, -65.1) * mm});
            skArc(sketch, "E52.24.1", {"start": v(-3.99, -63.37) * mm, "mid": v(-4.3, -62.24) * mm, "end": v(-4.71, -61.14) * mm});
            skArc(sketch, "E52.24.2", {"start": v(-7.96, -63) * mm, "mid": v(-7.43, -61.95) * mm, "end": v(-6.83, -60.94) * mm});
            skLineSegment(sketch, "E52.24.3", {"start": v(-7.96, -63) * mm, "end": v(-8.12, -64.72) * mm});
            skArc(sketch, "E52.24.4", {"start": v(-6.1, -60.59) * mm, "mid": v(-6.51, -60.67) * mm, "end": v(-6.83, -60.94) * mm});
            skLineSegment(sketch, "E52.24.5", {"start": v(-6.1, -60.59) * mm, "end": v(-5.73, -60.62) * mm});
            skLineSegment(sketch, "E52.24.6", {"start": v(-5.36, -60.66) * mm, "end": v(-5.73, -60.62) * mm});
            skArc(sketch, "E52.24.7", {"start": v(-4.71, -61.14) * mm, "mid": v(-4.97, -60.81) * mm, "end": v(-5.36, -60.66) * mm});
            skArc(sketch, "E52.24.8", {"start": v(-9.01, -65.42) * mm, "mid": v(-8.42, -65.26) * mm, "end": v(-8.12, -64.72) * mm});
            skArc(sketch, "E52.24.9", {"start": v(-4.15, -65.1) * mm, "mid": v(-3.96, -65.68) * mm, "end": v(-3.4, -65.95) * mm});
            skLineSegment(sketch, "E52.25.0", {"start": v(3.99, -63.37) * mm, "end": v(4.04, -65.1) * mm});
            skArc(sketch, "E52.25.1", {"start": v(3.99, -63.37) * mm, "mid": v(3.53, -62.3) * mm, "end": v(2.99, -61.25) * mm});
            skArc(sketch, "E52.25.2", {"start": v(0, -63.5) * mm, "mid": v(0.4, -62.4) * mm, "end": v(0.87, -61.32) * mm});
            skLineSegment(sketch, "E52.25.3", {"start": v(0, -63.5) * mm, "end": v(0.05, -65.22) * mm});
            skArc(sketch, "E52.25.4", {"start": v(1.54, -60.88) * mm, "mid": v(1.14, -61) * mm, "end": v(0.87, -61.32) * mm});
            skLineSegment(sketch, "E52.25.5", {"start": v(1.54, -60.88) * mm, "end": v(1.91, -60.86) * mm});
            skLineSegment(sketch, "E52.25.6", {"start": v(2.29, -60.85) * mm, "end": v(1.91, -60.86) * mm});
            skArc(sketch, "E52.25.7", {"start": v(2.99, -61.25) * mm, "mid": v(2.7, -60.96) * mm, "end": v(2.29, -60.85) * mm});
            skArc(sketch, "E52.25.8", {"start": v(-0.74, -66.04) * mm, "mid": v(-0.17, -65.8) * mm, "end": v(0.05, -65.22) * mm});
            skArc(sketch, "E52.25.9", {"start": v(4.04, -65.1) * mm, "mid": v(4.3, -65.66) * mm, "end": v(4.89, -65.86) * mm});
            skLineSegment(sketch, "E52.26.0", {"start": v(11.9, -62.37) * mm, "end": v(12.17, -64.08) * mm});
            skArc(sketch, "E52.26.1", {"start": v(11.9, -62.37) * mm, "mid": v(11.3, -61.36) * mm, "end": v(10.64, -60.4) * mm});
            skArc(sketch, "E52.26.2", {"start": v(7.96, -63) * mm, "mid": v(8.2, -61.85) * mm, "end": v(8.54, -60.73) * mm});
            skLineSegment(sketch, "E52.26.3", {"start": v(7.96, -63) * mm, "end": v(8.23, -64.7) * mm});
            skArc(sketch, "E52.26.4", {"start": v(9.16, -60.2) * mm, "mid": v(8.78, -60.38) * mm, "end": v(8.54, -60.73) * mm});
            skLineSegment(sketch, "E52.26.5", {"start": v(9.16, -60.2) * mm, "end": v(9.53, -60.14) * mm});
            skLineSegment(sketch, "E52.26.6", {"start": v(9.9, -60.09) * mm, "end": v(9.53, -60.14) * mm});
            skArc(sketch, "E52.26.7", {"start": v(10.64, -60.4) * mm, "mid": v(10.3, -60.14) * mm, "end": v(9.9, -60.09) * mm});
            skArc(sketch, "E52.26.8", {"start": v(7.54, -65.6) * mm, "mid": v(8.08, -65.3) * mm, "end": v(8.23, -64.7) * mm});
            skArc(sketch, "E52.26.9", {"start": v(12.17, -64.08) * mm, "mid": v(12.5, -64.6) * mm, "end": v(13.1, -64.73) * mm});
            skLineSegment(sketch, "E52.27.0", {"start": v(19.62, -60.39) * mm, "end": v(20.1, -62.05) * mm});
            skArc(sketch, "E52.27.1", {"start": v(19.62, -60.39) * mm, "mid": v(18.9, -59.46) * mm, "end": v(18.13, -58.58) * mm});
            skArc(sketch, "E52.27.2", {"start": v(15.8, -61.5) * mm, "mid": v(15.9, -60.33) * mm, "end": v(16.09, -59.18) * mm});
            skLineSegment(sketch, "E52.27.3", {"start": v(15.8, -61.5) * mm, "end": v(16.27, -63.16) * mm});
            skArc(sketch, "E52.27.4", {"start": v(16.63, -58.58) * mm, "mid": v(16.28, -58.8) * mm, "end": v(16.09, -59.18) * mm});
            skLineSegment(sketch, "E52.27.5", {"start": v(16.63, -58.58) * mm, "end": v(16.99, -58.47) * mm});
            skLineSegment(sketch, "E52.27.6", {"start": v(17.35, -58.37) * mm, "end": v(16.99, -58.47) * mm});
            skArc(sketch, "E52.27.7", {"start": v(18.13, -58.58) * mm, "mid": v(17.77, -58.37) * mm, "end": v(17.35, -58.37) * mm});
            skArc(sketch, "E52.27.8", {"start": v(15.7, -64.15) * mm, "mid": v(16.2, -63.77) * mm, "end": v(16.27, -63.16) * mm});
            skArc(sketch, "E52.27.9", {"start": v(20.1, -62.05) * mm, "mid": v(20.5, -62.53) * mm, "end": v(21.11, -62.57) * mm});
            skLineSegment(sketch, "E52.28.0", {"start": v(27.04, -57.45) * mm, "end": v(27.72, -59.04) * mm});
            skArc(sketch, "E52.28.1", {"start": v(27.04, -57.45) * mm, "mid": v(26.2, -56.62) * mm, "end": v(25.32, -55.85) * mm});
            skArc(sketch, "E52.28.2", {"start": v(23.37, -59.04) * mm, "mid": v(23.33, -57.87) * mm, "end": v(23.38, -56.7) * mm});
            skLineSegment(sketch, "E52.28.3", {"start": v(23.37, -59.04) * mm, "end": v(24.06, -60.62) * mm});
            skArc(sketch, "E52.28.4", {"start": v(23.84, -56.03) * mm, "mid": v(23.52, -56.3) * mm, "end": v(23.38, -56.7) * mm});
            skLineSegment(sketch, "E52.28.5", {"start": v(23.84, -56.03) * mm, "end": v(24.18, -55.88) * mm});
            skLineSegment(sketch, "E52.28.6", {"start": v(24.53, -55.74) * mm, "end": v(24.18, -55.88) * mm});
            skArc(sketch, "E52.28.7", {"start": v(25.32, -55.85) * mm, "mid": v(24.94, -55.68) * mm, "end": v(24.53, -55.74) * mm});
            skArc(sketch, "E52.28.8", {"start": v(23.62, -61.67) * mm, "mid": v(24.06, -61.24) * mm, "end": v(24.06, -60.62) * mm});
            skArc(sketch, "E52.28.9", {"start": v(27.72, -59.04) * mm, "mid": v(28.17, -59.46) * mm, "end": v(28.79, -59.44) * mm});
            skLineSegment(sketch, "E52.29.0", {"start": v(34.02, -53.61) * mm, "end": v(34.9, -55.1) * mm});
            skArc(sketch, "E52.29.1", {"start": v(34.02, -53.61) * mm, "mid": v(33.1, -52.89) * mm, "end": v(32.12, -52.24) * mm});
            skArc(sketch, "E52.29.2", {"start": v(30.59, -55.64) * mm, "mid": v(30.4, -54.49) * mm, "end": v(30.3, -53.32) * mm});
            skLineSegment(sketch, "E52.29.3", {"start": v(30.59, -55.64) * mm, "end": v(31.47, -57.13) * mm});
            skArc(sketch, "E52.29.4", {"start": v(30.68, -52.6) * mm, "mid": v(30.39, -52.9) * mm, "end": v(30.3, -53.32) * mm});
            skLineSegment(sketch, "E52.29.5", {"start": v(30.68, -52.6) * mm, "end": v(31, -52.4) * mm});
            skLineSegment(sketch, "E52.29.6", {"start": v(31.32, -52.22) * mm, "end": v(31, -52.4) * mm});
            skArc(sketch, "E52.29.7", {"start": v(32.12, -52.24) * mm, "mid": v(31.72, -52.12) * mm, "end": v(31.32, -52.22) * mm});
            skArc(sketch, "E52.29.8", {"start": v(31.16, -58.22) * mm, "mid": v(31.55, -57.74) * mm, "end": v(31.47, -57.13) * mm});
            skArc(sketch, "E52.29.9", {"start": v(34.9, -55.1) * mm, "mid": v(35.4, -55.47) * mm, "end": v(36, -55.36) * mm});
            skLineSegment(sketch, "E52.30.0", {"start": v(40.47, -48.93) * mm, "end": v(41.53, -50.3) * mm});
            skArc(sketch, "E52.30.1", {"start": v(40.47, -48.93) * mm, "mid": v(39.47, -48.32) * mm, "end": v(38.42, -47.8) * mm});
            skArc(sketch, "E52.30.2", {"start": v(37.32, -51.37) * mm, "mid": v(37, -50.25) * mm, "end": v(36.74, -49.1) * mm});
            skLineSegment(sketch, "E52.30.3", {"start": v(37.32, -51.37) * mm, "end": v(38.38, -52.74) * mm});
            skArc(sketch, "E52.30.4", {"start": v(37.03, -48.34) * mm, "mid": v(36.78, -48.68) * mm, "end": v(36.74, -49.1) * mm});
            skLineSegment(sketch, "E52.30.5", {"start": v(37.03, -48.34) * mm, "end": v(37.32, -48.11) * mm});
            skLineSegment(sketch, "E52.30.6", {"start": v(37.62, -47.89) * mm, "end": v(37.32, -48.11) * mm});
            skArc(sketch, "E52.30.7", {"start": v(38.42, -47.8) * mm, "mid": v(38, -47.73) * mm, "end": v(37.62, -47.89) * mm});
            skArc(sketch, "E52.30.8", {"start": v(38.21, -53.86) * mm, "mid": v(38.54, -53.33) * mm, "end": v(38.38, -52.74) * mm});
            skArc(sketch, "E52.30.9", {"start": v(41.53, -50.3) * mm, "mid": v(42.07, -50.6) * mm, "end": v(42.66, -50.4) * mm});
            skLineSegment(sketch, "E52.31.0", {"start": v(46.29, -43.47) * mm, "end": v(47.5, -44.69) * mm});
            skArc(sketch, "E52.31.1", {"start": v(46.29, -43.47) * mm, "mid": v(45.21, -43) * mm, "end": v(44.1, -42.6) * mm});
            skArc(sketch, "E52.31.2", {"start": v(43.47, -46.29) * mm, "mid": v(43, -45.21) * mm, "end": v(42.6, -44.1) * mm});
            skLineSegment(sketch, "E52.31.3", {"start": v(43.47, -46.29) * mm, "end": v(44.69, -47.5) * mm});
            skArc(sketch, "E52.31.4", {"start": v(42.8, -43.32) * mm, "mid": v(42.6, -43.69) * mm, "end": v(42.6, -44.1) * mm});
            skLineSegment(sketch, "E52.31.5", {"start": v(42.8, -43.32) * mm, "end": v(43.06, -43.06) * mm});
            skLineSegment(sketch, "E52.31.6", {"start": v(43.32, -42.8) * mm, "end": v(43.06, -43.06) * mm});
            skArc(sketch, "E52.31.7", {"start": v(44.1, -42.6) * mm, "mid": v(43.69, -42.6) * mm, "end": v(43.32, -42.8) * mm});
            skArc(sketch, "E52.31.8", {"start": v(44.66, -48.65) * mm, "mid": v(44.92, -48.08) * mm, "end": v(44.69, -47.5) * mm});
            skArc(sketch, "E52.31.9", {"start": v(47.5, -44.69) * mm, "mid": v(48.08, -44.92) * mm, "end": v(48.65, -44.66) * mm});
            skLineSegment(sketch, "E52.32.0", {"start": v(51.37, -37.32) * mm, "end": v(52.74, -38.38) * mm});
            skArc(sketch, "E52.32.1", {"start": v(51.37, -37.32) * mm, "mid": v(50.25, -37) * mm, "end": v(49.1, -36.74) * mm});
            skArc(sketch, "E52.32.2", {"start": v(48.93, -40.47) * mm, "mid": v(48.32, -39.47) * mm, "end": v(47.8, -38.42) * mm});
            skLineSegment(sketch, "E52.32.3", {"start": v(48.93, -40.47) * mm, "end": v(50.3, -41.53) * mm});
            skArc(sketch, "E52.32.4", {"start": v(47.89, -37.62) * mm, "mid": v(47.73, -38) * mm, "end": v(47.8, -38.42) * mm});
            skLineSegment(sketch, "E52.32.5", {"start": v(47.89, -37.62) * mm, "end": v(48.11, -37.32) * mm});
            skLineSegment(sketch, "E52.32.6", {"start": v(48.34, -37.03) * mm, "end": v(48.11, -37.32) * mm});
            skArc(sketch, "E52.32.7", {"start": v(49.1, -36.74) * mm, "mid": v(48.68, -36.78) * mm, "end": v(48.34, -37.03) * mm});
            skArc(sketch, "E52.32.8", {"start": v(50.4, -42.66) * mm, "mid": v(50.6, -42.07) * mm, "end": v(50.3, -41.53) * mm});
            skArc(sketch, "E52.32.9", {"start": v(52.74, -38.38) * mm, "mid": v(53.33, -38.54) * mm, "end": v(53.86, -38.21) * mm});
            skLineSegment(sketch, "E52.33.0", {"start": v(55.64, -30.59) * mm, "end": v(57.13, -31.47) * mm});
            skArc(sketch, "E52.33.1", {"start": v(55.64, -30.59) * mm, "mid": v(54.49, -30.4) * mm, "end": v(53.32, -30.3) * mm});
            skArc(sketch, "E52.33.2", {"start": v(53.61, -34.02) * mm, "mid": v(52.89, -33.1) * mm, "end": v(52.24, -32.12) * mm});
            skLineSegment(sketch, "E52.33.3", {"start": v(53.61, -34.02) * mm, "end": v(55.1, -34.9) * mm});
            skArc(sketch, "E52.33.4", {"start": v(52.22, -31.32) * mm, "mid": v(52.12, -31.72) * mm, "end": v(52.24, -32.12) * mm});
            skLineSegment(sketch, "E52.33.5", {"start": v(52.22, -31.32) * mm, "end": v(52.4, -31) * mm});
            skLineSegment(sketch, "E52.33.6", {"start": v(52.6, -30.68) * mm, "end": v(52.4, -31) * mm});
            skArc(sketch, "E52.33.7", {"start": v(53.32, -30.3) * mm, "mid": v(52.9, -30.39) * mm, "end": v(52.6, -30.68) * mm});
            skArc(sketch, "E52.33.8", {"start": v(55.36, -36) * mm, "mid": v(55.47, -35.4) * mm, "end": v(55.1, -34.9) * mm});
            skArc(sketch, "E52.33.9", {"start": v(57.13, -31.47) * mm, "mid": v(57.74, -31.55) * mm, "end": v(58.22, -31.16) * mm});
            skLineSegment(sketch, "E52.34.0", {"start": v(59.04, -23.37) * mm, "end": v(60.62, -24.06) * mm});
            skArc(sketch, "E52.34.1", {"start": v(59.04, -23.37) * mm, "mid": v(57.87, -23.33) * mm, "end": v(56.7, -23.38) * mm});
            skArc(sketch, "E52.34.2", {"start": v(57.45, -27.04) * mm, "mid": v(56.62, -26.2) * mm, "end": v(55.85, -25.32) * mm});
            skLineSegment(sketch, "E52.34.3", {"start": v(57.45, -27.04) * mm, "end": v(59.04, -27.72) * mm});
            skArc(sketch, "E52.34.4", {"start": v(55.74, -24.53) * mm, "mid": v(55.68, -24.94) * mm, "end": v(55.85, -25.32) * mm});
            skLineSegment(sketch, "E52.34.5", {"start": v(55.74, -24.53) * mm, "end": v(55.88, -24.18) * mm});
            skLineSegment(sketch, "E52.34.6", {"start": v(56.03, -23.84) * mm, "end": v(55.88, -24.18) * mm});
            skArc(sketch, "E52.34.7", {"start": v(56.7, -23.38) * mm, "mid": v(56.3, -23.52) * mm, "end": v(56.03, -23.84) * mm});
            skArc(sketch, "E52.34.8", {"start": v(59.44, -28.79) * mm, "mid": v(59.46, -28.17) * mm, "end": v(59.04, -27.72) * mm});
            skArc(sketch, "E52.34.9", {"start": v(60.62, -24.06) * mm, "mid": v(61.24, -24.06) * mm, "end": v(61.67, -23.62) * mm});
            skLineSegment(sketch, "E52.35.0", {"start": v(61.5, -15.8) * mm, "end": v(63.16, -16.27) * mm});
            skArc(sketch, "E52.35.1", {"start": v(61.5, -15.8) * mm, "mid": v(60.33, -15.9) * mm, "end": v(59.18, -16.09) * mm});
            skArc(sketch, "E52.35.2", {"start": v(60.39, -19.62) * mm, "mid": v(59.46, -18.9) * mm, "end": v(58.58, -18.13) * mm});
            skLineSegment(sketch, "E52.35.3", {"start": v(60.39, -19.62) * mm, "end": v(62.05, -20.1) * mm});
            skArc(sketch, "E52.35.4", {"start": v(58.37, -17.35) * mm, "mid": v(58.37, -17.77) * mm, "end": v(58.58, -18.13) * mm});
            skLineSegment(sketch, "E52.35.5", {"start": v(58.37, -17.35) * mm, "end": v(58.47, -16.99) * mm});
            skLineSegment(sketch, "E52.35.6", {"start": v(58.58, -16.63) * mm, "end": v(58.47, -16.99) * mm});
            skArc(sketch, "E52.35.7", {"start": v(59.18, -16.09) * mm, "mid": v(58.8, -16.28) * mm, "end": v(58.58, -16.63) * mm});
            skArc(sketch, "E52.35.8", {"start": v(62.57, -21.11) * mm, "mid": v(62.53, -20.5) * mm, "end": v(62.05, -20.1) * mm});
            skArc(sketch, "E52.35.9", {"start": v(63.16, -16.27) * mm, "mid": v(63.77, -16.2) * mm, "end": v(64.15, -15.7) * mm});
            skLineSegment(sketch, "E52.36.0", {"start": v(63, -7.96) * mm, "end": v(64.7, -8.23) * mm});
            skArc(sketch, "E52.36.1", {"start": v(63, -7.96) * mm, "mid": v(61.85, -8.2) * mm, "end": v(60.73, -8.54) * mm});
            skArc(sketch, "E52.36.2", {"start": v(62.37, -11.9) * mm, "mid": v(61.36, -11.3) * mm, "end": v(60.4, -10.64) * mm});
            skLineSegment(sketch, "E52.36.3", {"start": v(62.37, -11.9) * mm, "end": v(64.08, -12.17) * mm});
            skArc(sketch, "E52.36.4", {"start": v(60.09, -9.9) * mm, "mid": v(60.14, -10.3) * mm, "end": v(60.4, -10.64) * mm});
            skLineSegment(sketch, "E52.36.5", {"start": v(60.09, -9.9) * mm, "end": v(60.14, -9.53) * mm});
            skLineSegment(sketch, "E52.36.6", {"start": v(60.2, -9.16) * mm, "end": v(60.14, -9.53) * mm});
            skArc(sketch, "E52.36.7", {"start": v(60.73, -8.54) * mm, "mid": v(60.38, -8.78) * mm, "end": v(60.2, -9.16) * mm});
            skArc(sketch, "E52.36.8", {"start": v(64.73, -13.1) * mm, "mid": v(64.6, -12.5) * mm, "end": v(64.08, -12.17) * mm});
            skArc(sketch, "E52.36.9", {"start": v(64.7, -8.23) * mm, "mid": v(65.3, -8.08) * mm, "end": v(65.6, -7.54) * mm});
            skLineSegment(sketch, "E52.37.0", {"start": v(63.5, 0) * mm, "end": v(65.22, -0.05) * mm});
            skArc(sketch, "E52.37.1", {"start": v(63.5, 0) * mm, "mid": v(62.4, -0.4) * mm, "end": v(61.32, -0.87) * mm});
            skArc(sketch, "E52.37.2", {"start": v(63.37, -3.99) * mm, "mid": v(62.3, -3.53) * mm, "end": v(61.25, -2.99) * mm});
            skLineSegment(sketch, "E52.37.3", {"start": v(63.37, -3.99) * mm, "end": v(65.1, -4.04) * mm});
            skArc(sketch, "E52.37.4", {"start": v(60.85, -2.29) * mm, "mid": v(60.96, -2.7) * mm, "end": v(61.25, -2.99) * mm});
            skLineSegment(sketch, "E52.37.5", {"start": v(60.85, -2.29) * mm, "end": v(60.86, -1.91) * mm});
            skLineSegment(sketch, "E52.37.6", {"start": v(60.88, -1.54) * mm, "end": v(60.86, -1.91) * mm});
            skArc(sketch, "E52.37.7", {"start": v(61.32, -0.87) * mm, "mid": v(61, -1.14) * mm, "end": v(60.88, -1.54) * mm});
            skArc(sketch, "E52.37.8", {"start": v(65.86, -4.89) * mm, "mid": v(65.66, -4.3) * mm, "end": v(65.1, -4.04) * mm});
            skArc(sketch, "E52.37.9", {"start": v(65.22, -0.05) * mm, "mid": v(65.8, 0.17) * mm, "end": v(66.04, 0.74) * mm});
            skLineSegment(sketch, "E52.38.0", {"start": v(63, 7.96) * mm, "end": v(64.72, 8.12) * mm});
            skArc(sketch, "E52.38.1", {"start": v(63, 7.96) * mm, "mid": v(61.95, 7.43) * mm, "end": v(60.94, 6.83) * mm});
            skArc(sketch, "E52.38.2", {"start": v(63.37, 3.99) * mm, "mid": v(62.24, 4.3) * mm, "end": v(61.14, 4.71) * mm});
            skLineSegment(sketch, "E52.38.3", {"start": v(63.37, 3.99) * mm, "end": v(65.1, 4.15) * mm});
            skArc(sketch, "E52.38.4", {"start": v(60.66, 5.36) * mm, "mid": v(60.81, 4.97) * mm, "end": v(61.14, 4.71) * mm});
            skLineSegment(sketch, "E52.38.5", {"start": v(60.66, 5.36) * mm, "end": v(60.62, 5.73) * mm});
            skLineSegment(sketch, "E52.38.6", {"start": v(60.59, 6.1) * mm, "end": v(60.62, 5.73) * mm});
            skArc(sketch, "E52.38.7", {"start": v(60.94, 6.83) * mm, "mid": v(60.67, 6.51) * mm, "end": v(60.59, 6.1) * mm});
            skArc(sketch, "E52.38.8", {"start": v(65.95, 3.4) * mm, "mid": v(65.68, 3.96) * mm, "end": v(65.1, 4.15) * mm});
            skArc(sketch, "E52.38.9", {"start": v(64.72, 8.12) * mm, "mid": v(65.26, 8.42) * mm, "end": v(65.42, 9.01) * mm});
            skLineSegment(sketch, "E52.39.0", {"start": v(61.5, 15.8) * mm, "end": v(63.19, 16.17) * mm});
            skArc(sketch, "E52.39.1", {"start": v(61.5, 15.8) * mm, "mid": v(60.53, 15.14) * mm, "end": v(59.6, 14.41) * mm});
            skArc(sketch, "E52.39.2", {"start": v(62.37, 11.9) * mm, "mid": v(61.21, 12.08) * mm, "end": v(60.07, 12.34) * mm});
            skLineSegment(sketch, "E52.39.3", {"start": v(62.37, 11.9) * mm, "end": v(64.06, 12.27) * mm});
            skArc(sketch, "E52.39.4", {"start": v(59.5, 12.92) * mm, "mid": v(59.7, 12.55) * mm, "end": v(60.07, 12.34) * mm});
            skLineSegment(sketch, "E52.39.5", {"start": v(59.5, 12.92) * mm, "end": v(59.42, 13.28) * mm});
            skLineSegment(sketch, "E52.39.6", {"start": v(59.35, 13.65) * mm, "end": v(59.42, 13.28) * mm});
            skArc(sketch, "E52.39.7", {"start": v(59.6, 14.41) * mm, "mid": v(59.37, 14.07) * mm, "end": v(59.35, 13.65) * mm});
            skArc(sketch, "E52.39.8", {"start": v(65, 11.65) * mm, "mid": v(64.67, 12.16) * mm, "end": v(64.06, 12.27) * mm});
            skArc(sketch, "E52.39.9", {"start": v(63.19, 16.17) * mm, "mid": v(63.7, 16.53) * mm, "end": v(63.78, 17.14) * mm});
            skLineSegment(sketch, "E52.40.0", {"start": v(59.04, 23.37) * mm, "end": v(60.66, 23.96) * mm});
            skArc(sketch, "E52.40.1", {"start": v(59.04, 23.37) * mm, "mid": v(58.15, 22.6) * mm, "end": v(57.33, 21.77) * mm});
            skArc(sketch, "E52.40.2", {"start": v(60.39, 19.62) * mm, "mid": v(59.22, 19.65) * mm, "end": v(58.05, 19.77) * mm});
            skLineSegment(sketch, "E52.40.3", {"start": v(60.39, 19.62) * mm, "end": v(62.01, 20.2) * mm});
            skArc(sketch, "E52.40.4", {"start": v(57.42, 20.28) * mm, "mid": v(57.67, 19.94) * mm, "end": v(58.05, 19.77) * mm});
            skLineSegment(sketch, "E52.40.5", {"start": v(57.42, 20.28) * mm, "end": v(57.29, 20.63) * mm});
            skLineSegment(sketch, "E52.40.6", {"start": v(57.17, 20.98) * mm, "end": v(57.29, 20.63) * mm});
            skArc(sketch, "E52.40.7", {"start": v(57.33, 21.77) * mm, "mid": v(57.14, 21.4) * mm, "end": v(57.17, 20.98) * mm});
            skArc(sketch, "E52.40.8", {"start": v(63.03, 19.7) * mm, "mid": v(62.63, 20.17) * mm, "end": v(62.01, 20.2) * mm});
            skArc(sketch, "E52.40.9", {"start": v(60.66, 23.96) * mm, "mid": v(61.12, 24.38) * mm, "end": v(61.13, 25) * mm});
            skLineSegment(sketch, "E52.41.0", {"start": v(55.64, 30.6) * mm, "end": v(57.18, 31.37) * mm});
            skArc(sketch, "E52.41.1", {"start": v(55.64, 30.6) * mm, "mid": v(54.86, 29.71) * mm, "end": v(54.15, 28.78) * mm});
            skArc(sketch, "E52.41.2", {"start": v(57.45, 27.04) * mm, "mid": v(56.29, 26.92) * mm, "end": v(55.11, 26.9) * mm});
            skLineSegment(sketch, "E52.41.3", {"start": v(57.45, 27.04) * mm, "end": v(59, 27.82) * mm});
            skArc(sketch, "E52.41.4", {"start": v(54.43, 27.31) * mm, "mid": v(54.71, 27) * mm, "end": v(55.11, 26.9) * mm});
            skLineSegment(sketch, "E52.41.5", {"start": v(54.43, 27.31) * mm, "end": v(54.25, 27.64) * mm});
            skLineSegment(sketch, "E52.41.6", {"start": v(54.09, 27.98) * mm, "end": v(54.25, 27.64) * mm});
            skArc(sketch, "E52.41.7", {"start": v(54.15, 28.78) * mm, "mid": v(54, 28.39) * mm, "end": v(54.09, 27.98) * mm});
            skArc(sketch, "E52.41.8", {"start": v(60.07, 27.45) * mm, "mid": v(59.6, 27.86) * mm, "end": v(59, 27.82) * mm});
            skArc(sketch, "E52.41.9", {"start": v(57.18, 31.37) * mm, "mid": v(57.58, 31.85) * mm, "end": v(57.51, 32.46) * mm});
            skLineSegment(sketch, "E52.42.0", {"start": v(51.37, 37.32) * mm, "end": v(52.8, 38.3) * mm});
            skArc(sketch, "E52.42.1", {"start": v(51.37, 37.32) * mm, "mid": v(50.7, 36.36) * mm, "end": v(50.12, 35.34) * mm});
            skArc(sketch, "E52.42.2", {"start": v(53.61, 34.02) * mm, "mid": v(52.47, 33.76) * mm, "end": v(51.3, 33.59) * mm});
            skLineSegment(sketch, "E52.42.3", {"start": v(53.61, 34.02) * mm, "end": v(55.04, 35) * mm});
            skArc(sketch, "E52.42.4", {"start": v(50.57, 33.92) * mm, "mid": v(50.9, 33.65) * mm, "end": v(51.3, 33.59) * mm});
            skLineSegment(sketch, "E52.42.5", {"start": v(50.57, 33.92) * mm, "end": v(50.36, 34.22) * mm});
            skLineSegment(sketch, "E52.42.6", {"start": v(50.15, 34.54) * mm, "end": v(50.36, 34.22) * mm});
            skArc(sketch, "E52.42.7", {"start": v(50.12, 35.34) * mm, "mid": v(50.02, 34.93) * mm, "end": v(50.15, 34.54) * mm});
            skArc(sketch, "E52.42.8", {"start": v(56.15, 34.76) * mm, "mid": v(55.65, 35.11) * mm, "end": v(55.04, 35) * mm});
            skArc(sketch, "E52.42.9", {"start": v(52.8, 38.3) * mm, "mid": v(53.13, 38.81) * mm, "end": v(52.99, 39.41) * mm});
            skLineSegment(sketch, "E52.43.0", {"start": v(46.29, 43.47) * mm, "end": v(47.58, 44.6) * mm});
            skArc(sketch, "E52.43.1", {"start": v(46.29, 43.47) * mm, "mid": v(45.75, 42.42) * mm, "end": v(45.3, 41.34) * mm});
            skArc(sketch, "E52.43.2", {"start": v(48.93, 40.47) * mm, "mid": v(47.82, 40.07) * mm, "end": v(46.7, 39.75) * mm});
            skLineSegment(sketch, "E52.43.3", {"start": v(48.93, 40.47) * mm, "end": v(50.22, 41.62) * mm});
            skArc(sketch, "E52.43.4", {"start": v(45.92, 39.99) * mm, "mid": v(46.28, 39.77) * mm, "end": v(46.7, 39.75) * mm});
            skLineSegment(sketch, "E52.43.5", {"start": v(45.92, 39.99) * mm, "end": v(45.67, 40.27) * mm});
            skLineSegment(sketch, "E52.43.6", {"start": v(45.43, 40.55) * mm, "end": v(45.67, 40.27) * mm});
            skArc(sketch, "E52.43.7", {"start": v(45.3, 41.34) * mm, "mid": v(45.25, 40.93) * mm, "end": v(45.43, 40.55) * mm});
            skArc(sketch, "E52.43.8", {"start": v(51.35, 41.52) * mm, "mid": v(50.8, 41.81) * mm, "end": v(50.22, 41.62) * mm});
            skArc(sketch, "E52.43.9", {"start": v(47.58, 44.6) * mm, "mid": v(47.85, 45.17) * mm, "end": v(47.63, 45.75) * mm});
            skLineSegment(sketch, "E52.44.0", {"start": v(40.47, 48.93) * mm, "end": v(41.62, 50.22) * mm});
            skArc(sketch, "E52.44.1", {"start": v(40.47, 48.93) * mm, "mid": v(40.07, 47.82) * mm, "end": v(39.75, 46.7) * mm});
            skArc(sketch, "E52.44.2", {"start": v(43.47, 46.29) * mm, "mid": v(42.42, 45.75) * mm, "end": v(41.34, 45.3) * mm});
            skLineSegment(sketch, "E52.44.3", {"start": v(43.47, 46.29) * mm, "end": v(44.6, 47.58) * mm});
            skArc(sketch, "E52.44.4", {"start": v(40.55, 45.43) * mm, "mid": v(40.93, 45.25) * mm, "end": v(41.34, 45.3) * mm});
            skLineSegment(sketch, "E52.44.5", {"start": v(40.55, 45.43) * mm, "end": v(40.27, 45.67) * mm});
            skLineSegment(sketch, "E52.44.6", {"start": v(39.99, 45.92) * mm, "end": v(40.27, 45.67) * mm});
            skArc(sketch, "E52.44.7", {"start": v(39.75, 46.7) * mm, "mid": v(39.77, 46.28) * mm, "end": v(39.99, 45.92) * mm});
            skArc(sketch, "E52.44.8", {"start": v(45.75, 47.63) * mm, "mid": v(45.17, 47.85) * mm, "end": v(44.6, 47.58) * mm});
            skArc(sketch, "E52.44.9", {"start": v(41.62, 50.22) * mm, "mid": v(41.81, 50.8) * mm, "end": v(41.52, 51.35) * mm});
            skLineSegment(sketch, "E52.45.0", {"start": v(34.02, 53.61) * mm, "end": v(35, 55.04) * mm});
            skArc(sketch, "E52.45.1", {"start": v(34.02, 53.61) * mm, "mid": v(33.76, 52.47) * mm, "end": v(33.59, 51.3) * mm});
            skArc(sketch, "E52.45.2", {"start": v(37.32, 51.37) * mm, "mid": v(36.36, 50.7) * mm, "end": v(35.34, 50.12) * mm});
            skLineSegment(sketch, "E52.45.3", {"start": v(37.32, 51.37) * mm, "end": v(38.3, 52.8) * mm});
            skArc(sketch, "E52.45.4", {"start": v(34.54, 50.15) * mm, "mid": v(34.93, 50.02) * mm, "end": v(35.34, 50.12) * mm});
            skLineSegment(sketch, "E52.45.5", {"start": v(34.54, 50.15) * mm, "end": v(34.22, 50.36) * mm});
            skLineSegment(sketch, "E52.45.6", {"start": v(33.92, 50.57) * mm, "end": v(34.22, 50.36) * mm});
            skArc(sketch, "E52.45.7", {"start": v(33.59, 51.3) * mm, "mid": v(33.65, 50.9) * mm, "end": v(33.92, 50.57) * mm});
            skArc(sketch, "E52.45.8", {"start": v(39.41, 52.99) * mm, "mid": v(38.81, 53.13) * mm, "end": v(38.3, 52.8) * mm});
            skArc(sketch, "E52.45.9", {"start": v(35, 55.04) * mm, "mid": v(35.11, 55.65) * mm, "end": v(34.76, 56.15) * mm});
            skLineSegment(sketch, "E52.46.0", {"start": v(27.04, 57.45) * mm, "end": v(27.82, 59) * mm});
            skArc(sketch, "E52.46.1", {"start": v(27.04, 57.45) * mm, "mid": v(26.92, 56.29) * mm, "end": v(26.9, 55.11) * mm});
            skArc(sketch, "E52.46.2", {"start": v(30.6, 55.64) * mm, "mid": v(29.71, 54.86) * mm, "end": v(28.78, 54.15) * mm});
            skLineSegment(sketch, "E52.46.3", {"start": v(30.6, 55.64) * mm, "end": v(31.37, 57.18) * mm});
            skArc(sketch, "E52.46.4", {"start": v(27.98, 54.09) * mm, "mid": v(28.39, 54) * mm, "end": v(28.78, 54.15) * mm});
            skLineSegment(sketch, "E52.46.5", {"start": v(27.98, 54.09) * mm, "end": v(27.64, 54.25) * mm});
            skLineSegment(sketch, "E52.46.6", {"start": v(27.31, 54.43) * mm, "end": v(27.64, 54.25) * mm});
            skArc(sketch, "E52.46.7", {"start": v(26.9, 55.11) * mm, "mid": v(27, 54.71) * mm, "end": v(27.31, 54.43) * mm});
            skArc(sketch, "E52.46.8", {"start": v(32.46, 57.51) * mm, "mid": v(31.85, 57.58) * mm, "end": v(31.37, 57.18) * mm});
            skArc(sketch, "E52.46.9", {"start": v(27.82, 59) * mm, "mid": v(27.86, 59.6) * mm, "end": v(27.45, 60.07) * mm});
            skLineSegment(sketch, "E52.47.0", {"start": v(19.62, 60.39) * mm, "end": v(20.2, 62.01) * mm});
            skArc(sketch, "E52.47.1", {"start": v(19.62, 60.39) * mm, "mid": v(19.65, 59.22) * mm, "end": v(19.77, 58.05) * mm});
            skArc(sketch, "E52.47.2", {"start": v(23.37, 59.04) * mm, "mid": v(22.6, 58.15) * mm, "end": v(21.77, 57.33) * mm});
            skLineSegment(sketch, "E52.47.3", {"start": v(23.37, 59.04) * mm, "end": v(23.96, 60.66) * mm});
            skArc(sketch, "E52.47.4", {"start": v(20.98, 57.17) * mm, "mid": v(21.4, 57.14) * mm, "end": v(21.77, 57.33) * mm});
            skLineSegment(sketch, "E52.47.5", {"start": v(20.98, 57.17) * mm, "end": v(20.63, 57.29) * mm});
            skLineSegment(sketch, "E52.47.6", {"start": v(20.28, 57.42) * mm, "end": v(20.63, 57.29) * mm});
            skArc(sketch, "E52.47.7", {"start": v(19.77, 58.05) * mm, "mid": v(19.94, 57.67) * mm, "end": v(20.28, 57.42) * mm});
            skArc(sketch, "E52.47.8", {"start": v(25, 61.13) * mm, "mid": v(24.38, 61.12) * mm, "end": v(23.96, 60.66) * mm});
            skArc(sketch, "E52.47.9", {"start": v(20.2, 62.01) * mm, "mid": v(20.17, 62.63) * mm, "end": v(19.7, 63.03) * mm});
            skLineSegment(sketch, "E52.48.0", {"start": v(11.9, 62.37) * mm, "end": v(12.27, 64.06) * mm});
            skArc(sketch, "E52.48.1", {"start": v(11.9, 62.37) * mm, "mid": v(12.08, 61.21) * mm, "end": v(12.34, 60.07) * mm});
            skArc(sketch, "E52.48.2", {"start": v(15.8, 61.5) * mm, "mid": v(15.14, 60.53) * mm, "end": v(14.41, 59.6) * mm});
            skLineSegment(sketch, "E52.48.3", {"start": v(15.8, 61.5) * mm, "end": v(16.17, 63.19) * mm});
            skArc(sketch, "E52.48.4", {"start": v(13.65, 59.35) * mm, "mid": v(14.07, 59.37) * mm, "end": v(14.41, 59.6) * mm});
            skLineSegment(sketch, "E52.48.5", {"start": v(13.65, 59.35) * mm, "end": v(13.28, 59.42) * mm});
            skLineSegment(sketch, "E52.48.6", {"start": v(12.92, 59.5) * mm, "end": v(13.28, 59.42) * mm});
            skArc(sketch, "E52.48.7", {"start": v(12.34, 60.07) * mm, "mid": v(12.55, 59.7) * mm, "end": v(12.92, 59.5) * mm});
            skArc(sketch, "E52.48.8", {"start": v(17.14, 63.78) * mm, "mid": v(16.53, 63.7) * mm, "end": v(16.17, 63.19) * mm});
            skArc(sketch, "E52.48.9", {"start": v(12.27, 64.06) * mm, "mid": v(12.16, 64.67) * mm, "end": v(11.65, 65) * mm});
            skLineSegment(sketch, "E52.49.0", {"start": v(3.99, 63.37) * mm, "end": v(4.15, 65.1) * mm});
            skArc(sketch, "E52.49.1", {"start": v(3.99, 63.37) * mm, "mid": v(4.3, 62.24) * mm, "end": v(4.71, 61.14) * mm});
            skArc(sketch, "E52.49.2", {"start": v(7.96, 63) * mm, "mid": v(7.43, 61.95) * mm, "end": v(6.83, 60.94) * mm});
            skLineSegment(sketch, "E52.49.3", {"start": v(7.96, 63) * mm, "end": v(8.12, 64.72) * mm});
            skArc(sketch, "E52.49.4", {"start": v(6.1, 60.59) * mm, "mid": v(6.51, 60.67) * mm, "end": v(6.83, 60.94) * mm});
            skLineSegment(sketch, "E52.49.5", {"start": v(6.1, 60.59) * mm, "end": v(5.73, 60.62) * mm});
            skLineSegment(sketch, "E52.49.6", {"start": v(5.36, 60.66) * mm, "end": v(5.73, 60.62) * mm});
            skArc(sketch, "E52.49.7", {"start": v(4.71, 61.14) * mm, "mid": v(4.97, 60.81) * mm, "end": v(5.36, 60.66) * mm});
            skArc(sketch, "E52.49.8", {"start": v(9.01, 65.42) * mm, "mid": v(8.42, 65.26) * mm, "end": v(8.12, 64.72) * mm});
            skArc(sketch, "E52.49.9", {"start": v(4.15, 65.1) * mm, "mid": v(3.96, 65.68) * mm, "end": v(3.4, 65.95) * mm});
            skArc(sketch, "E53.trimOffspring", {"start": v(-13.1, 64.73) * mm, "mid": v(-14.4, 64.45) * mm, "end": v(-15.7, 64.15) * mm});
            skArc(sketch, "E54.trimOffspring", {"start": v(3.4, 65.95) * mm, "mid": v(2.07, 66) * mm, "end": v(0.74, 66.04) * mm});
            skArc(sketch, "E55.trimOffspring", {"start": v(11.65, 65) * mm, "mid": v(10.33, 65.23) * mm, "end": v(9.01, 65.42) * mm});
            skArc(sketch, "E56.trimOffspring", {"start": v(19.7, 63.03) * mm, "mid": v(18.42, 63.42) * mm, "end": v(17.14, 63.78) * mm});
            skArc(sketch, "E57.trimOffspring", {"start": v(27.45, 60.07) * mm, "mid": v(26.23, 60.6) * mm, "end": v(25, 61.13) * mm});
            skArc(sketch, "E58.trimOffspring", {"start": v(34.76, 56.15) * mm, "mid": v(33.62, 56.84) * mm, "end": v(32.46, 57.51) * mm});
            skArc(sketch, "E59.trimOffspring", {"start": v(41.52, 51.35) * mm, "mid": v(40.48, 52.18) * mm, "end": v(39.41, 52.99) * mm});
            skArc(sketch, "E60.trimOffspring", {"start": v(47.63, 45.75) * mm, "mid": v(46.7, 46.7) * mm, "end": v(45.75, 47.63) * mm});
            skArc(sketch, "E61.trimOffspring", {"start": v(52.99, 39.41) * mm, "mid": v(52.18, 40.48) * mm, "end": v(51.35, 41.52) * mm});
            skArc(sketch, "E62.trimOffspring", {"start": v(57.51, 32.46) * mm, "mid": v(56.84, 33.62) * mm, "end": v(56.15, 34.76) * mm});
            skArc(sketch, "E63.trimOffspring", {"start": v(61.13, 25) * mm, "mid": v(60.6, 26.23) * mm, "end": v(60.07, 27.45) * mm});
            skArc(sketch, "E64.trimOffspring", {"start": v(63.78, 17.14) * mm, "mid": v(63.42, 18.42) * mm, "end": v(63.03, 19.7) * mm});
            skArc(sketch, "E65.trimOffspring", {"start": v(65.42, 9.01) * mm, "mid": v(65.23, 10.33) * mm, "end": v(65, 11.65) * mm});
            skArc(sketch, "E66.trimOffspring", {"start": v(-21.11, 62.57) * mm, "mid": v(-22.37, 62.14) * mm, "end": v(-23.62, 61.67) * mm});
            skArc(sketch, "E67.trimOffspring", {"start": v(-28.79, 59.44) * mm, "mid": v(-29.98, 58.84) * mm, "end": v(-31.16, 58.22) * mm});
            skArc(sketch, "E68.trimOffspring", {"start": v(-36, 55.36) * mm, "mid": v(-37.12, 54.62) * mm, "end": v(-38.21, 53.86) * mm});
            skArc(sketch, "E69.trimOffspring", {"start": v(-42.66, 50.4) * mm, "mid": v(-43.67, 49.54) * mm, "end": v(-44.66, 48.65) * mm});
            skArc(sketch, "E70.trimOffspring", {"start": v(-53.86, 38.21) * mm, "mid": v(-54.62, 37.12) * mm, "end": v(-55.36, 36) * mm});
            skArc(sketch, "E71.trimOffspring", {"start": v(-58.22, 31.16) * mm, "mid": v(-58.84, 29.98) * mm, "end": v(-59.44, 28.79) * mm});
            skArc(sketch, "E72.trimOffspring", {"start": v(-61.67, 23.62) * mm, "mid": v(-62.14, 22.37) * mm, "end": v(-62.57, 21.11) * mm});
            skArc(sketch, "E73.trimOffspring", {"start": v(-64.15, 15.7) * mm, "mid": v(-64.45, 14.4) * mm, "end": v(-64.73, 13.1) * mm});
            skArc(sketch, "E74.trimOffspring", {"start": v(-65.6, 7.54) * mm, "mid": v(-65.75, 6.21) * mm, "end": v(-65.86, 4.89) * mm});
            skArc(sketch, "E75.trimOffspring", {"start": v(-66.04, -0.74) * mm, "mid": v(-66, -2.07) * mm, "end": v(-65.95, -3.4) * mm});
            skArc(sketch, "E76.trimOffspring", {"start": v(-65.42, -9.01) * mm, "mid": v(-65.23, -10.33) * mm, "end": v(-65, -11.65) * mm});
            skArc(sketch, "E77.trimOffspring", {"start": v(-63.78, -17.14) * mm, "mid": v(-63.42, -18.42) * mm, "end": v(-63.03, -19.7) * mm});
            skArc(sketch, "E78.trimOffspring", {"start": v(-61.13, -25) * mm, "mid": v(-60.6, -26.23) * mm, "end": v(-60.07, -27.45) * mm});
            skArc(sketch, "E79.trimOffspring", {"start": v(66.04, 0.74) * mm, "mid": v(66, 2.07) * mm, "end": v(65.95, 3.4) * mm});
            skArc(sketch, "E80.trimOffspring", {"start": v(65.6, -7.54) * mm, "mid": v(65.75, -6.21) * mm, "end": v(65.86, -4.89) * mm});
            skArc(sketch, "E81.trimOffspring", {"start": v(64.15, -15.7) * mm, "mid": v(64.45, -14.4) * mm, "end": v(64.73, -13.1) * mm});
            skArc(sketch, "E82.trimOffspring", {"start": v(61.67, -23.62) * mm, "mid": v(62.14, -22.37) * mm, "end": v(62.57, -21.11) * mm});
            skArc(sketch, "E83.trimOffspring", {"start": v(58.22, -31.16) * mm, "mid": v(58.84, -29.98) * mm, "end": v(59.44, -28.79) * mm});
            skArc(sketch, "E84.trimOffspring", {"start": v(53.86, -38.21) * mm, "mid": v(54.62, -37.12) * mm, "end": v(55.36, -36) * mm});
            skArc(sketch, "E85.trimOffspring", {"start": v(48.65, -44.66) * mm, "mid": v(49.54, -43.67) * mm, "end": v(50.4, -42.66) * mm});
            skArc(sketch, "E86.trimOffspring", {"start": v(42.66, -50.4) * mm, "mid": v(43.67, -49.54) * mm, "end": v(44.66, -48.65) * mm});
            skArc(sketch, "E87.trimOffspring", {"start": v(36, -55.36) * mm, "mid": v(37.12, -54.62) * mm, "end": v(38.21, -53.86) * mm});
            skArc(sketch, "E88.trimOffspring", {"start": v(28.79, -59.44) * mm, "mid": v(29.98, -58.84) * mm, "end": v(31.16, -58.22) * mm});
            skArc(sketch, "E89.trimOffspring", {"start": v(21.11, -62.57) * mm, "mid": v(22.37, -62.14) * mm, "end": v(23.62, -61.67) * mm});
            skArc(sketch, "E90.trimOffspring", {"start": v(13.1, -64.73) * mm, "mid": v(14.4, -64.45) * mm, "end": v(15.7, -64.15) * mm});
            skArc(sketch, "E91.trimOffspring", {"start": v(4.89, -65.86) * mm, "mid": v(6.21, -65.75) * mm, "end": v(7.54, -65.6) * mm});
            skArc(sketch, "E92.trimOffspring", {"start": v(-3.4, -65.95) * mm, "mid": v(-2.07, -66) * mm, "end": v(-0.74, -66.04) * mm});
            skArc(sketch, "E93.trimOffspring", {"start": v(-11.65, -65) * mm, "mid": v(-10.33, -65.23) * mm, "end": v(-9.01, -65.42) * mm});
            skArc(sketch, "E94.trimOffspring", {"start": v(-19.7, -63.03) * mm, "mid": v(-18.42, -63.42) * mm, "end": v(-17.14, -63.78) * mm});
            skArc(sketch, "E95.trimOffspring", {"start": v(-27.45, -60.07) * mm, "mid": v(-26.23, -60.6) * mm, "end": v(-25, -61.13) * mm});
            skArc(sketch, "E96.trimOffspring", {"start": v(-34.76, -56.15) * mm, "mid": v(-33.62, -56.84) * mm, "end": v(-32.46, -57.51) * mm});
            skArc(sketch, "E97.trimOffspring", {"start": v(-41.52, -51.35) * mm, "mid": v(-40.48, -52.18) * mm, "end": v(-39.41, -52.99) * mm});
            skArc(sketch, "E98.trimOffspring", {"start": v(-47.63, -45.75) * mm, "mid": v(-46.7, -46.7) * mm, "end": v(-45.75, -47.63) * mm});
            skArc(sketch, "E99.trimOffspring", {"start": v(-52.99, -39.41) * mm, "mid": v(-52.18, -40.48) * mm, "end": v(-51.35, -41.52) * mm});
            skArc(sketch, "E100.trimOffspring", {"start": v(-57.51, -32.46) * mm, "mid": v(-56.84, -33.62) * mm, "end": v(-56.15, -34.76) * mm});
            skLineSegment(sketch, "E101", {"start": v(-50.4, 42.66) * mm, "end": v(-48.65, 44.66) * mm});
            skSolve(sketch);
        }
        {
            var Q0;
            Q0 = qSketchRegion(id + "F0", true);
            extrude(context, id + "F1", {"entities" : qUnion([Q0]), "depth" : 127 * mm});
        }
    });
